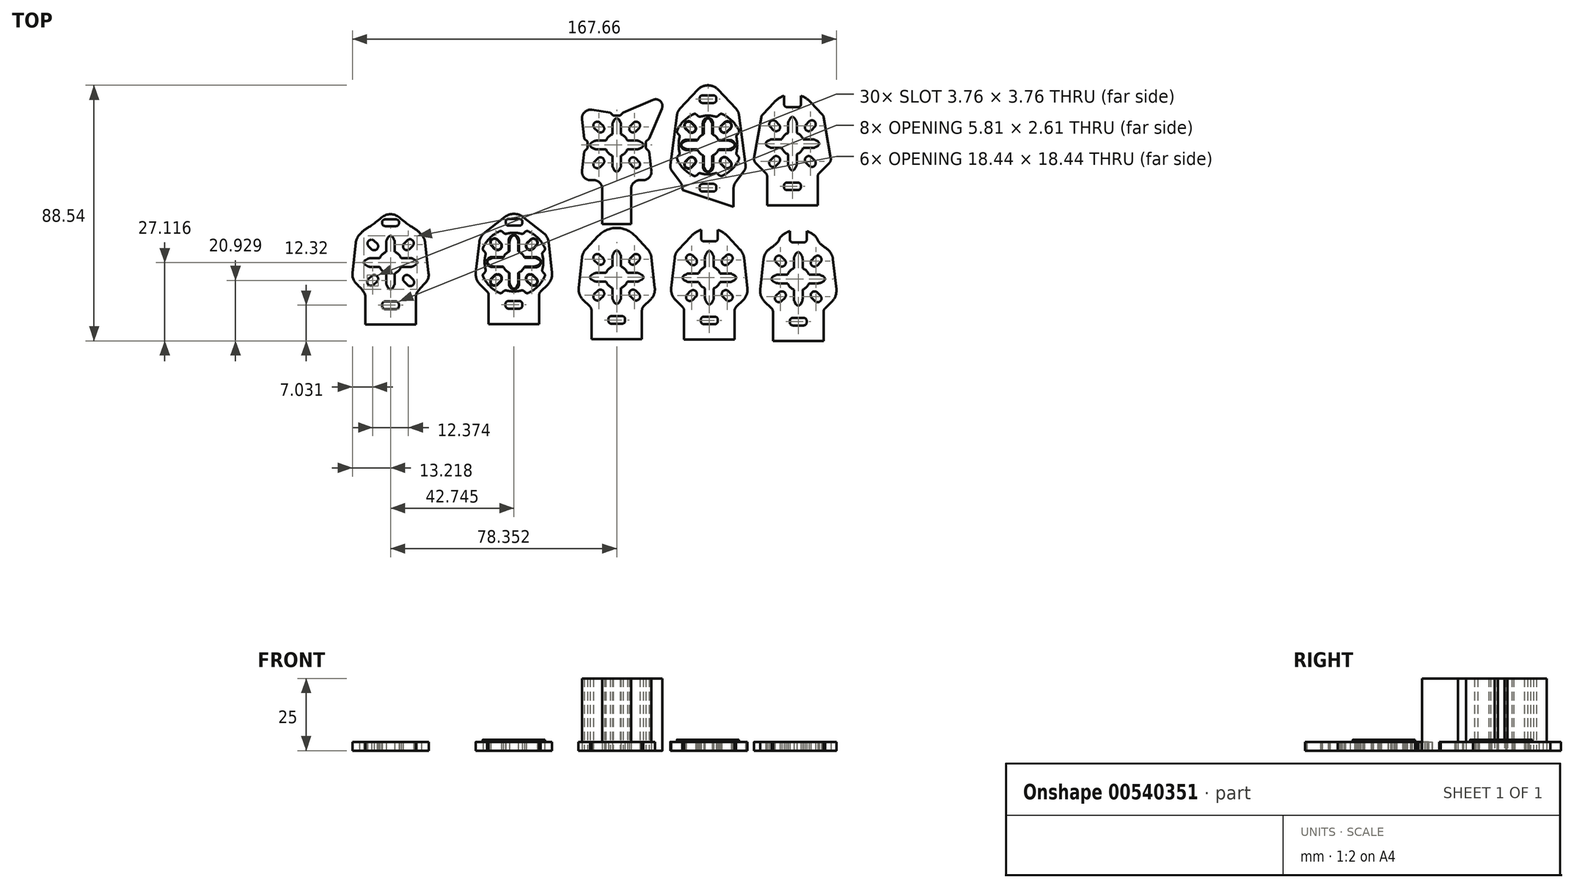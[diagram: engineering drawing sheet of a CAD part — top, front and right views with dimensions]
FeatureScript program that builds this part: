
annotation { "Feature Type Name" : "Feature", "Feature Type Description" : "" }
export const myFeature = defineFeature(function(context is Context, id is Id, definition is map)
    precondition{}
    {
        {
            var Q0;
            Q0=qCreatedBy(makeId("Top.planeOp"),FACE);
            var sketch = newSketch(context, id + "F0", { "sketchPlane" : qUnion([Q0])});
            skArc(sketch, "E0", {"start": v(6.61, -4.7) * mm, "mid": v(4.7, -4.7) * mm, "end": v(4.7, -6.61) * mm});
            skArc(sketch, "E1", {"start": v(5.76, -7.67) * mm, "mid": v(7.67, -7.67) * mm, "end": v(7.67, -5.76) * mm});
            skLineSegment(sketch, "E2", {"start": v(0, 0) * mm, "end": v(-21.23, -21.23) * mm, "construction": true});
            skLineSegment(sketch, "E3", {"start": v(4.7, -6.61) * mm, "end": v(5.76, -7.67) * mm});
            skLineSegment(sketch, "E4.MirrorCS", {"start": v(6.61, -4.7) * mm, "end": v(7.67, -5.76) * mm});
            skLineSegment(sketch, "E5.MirrorCS", {"start": v(-6.61, -4.7) * mm, "end": v(-7.67, -5.76) * mm});
            skArc(sketch, "E6.MirrorCS", {"start": v(-5.76, -7.67) * mm, "mid": v(-7.67, -7.67) * mm, "end": v(-7.67, -5.76) * mm});
            skLineSegment(sketch, "E7.MirrorCS", {"start": v(-4.7, -6.61) * mm, "end": v(-5.76, -7.67) * mm});
            skArc(sketch, "E8.MirrorCS", {"start": v(-6.61, -4.7) * mm, "mid": v(-4.7, -4.7) * mm, "end": v(-4.7, -6.61) * mm});
            skLineSegment(sketch, "E9.MirrorCS", {"start": v(-4.7, 6.61) * mm, "end": v(-5.76, 7.67) * mm});
            skLineSegment(sketch, "E10.MirrorCS", {"start": v(-6.61, 4.7) * mm, "end": v(-7.67, 5.76) * mm});
            skArc(sketch, "E11.MirrorCS", {"start": v(-6.61, 4.7) * mm, "mid": v(-4.7, 4.7) * mm, "end": v(-4.7, 6.61) * mm});
            skArc(sketch, "E12.MirrorCS", {"start": v(-5.76, 7.67) * mm, "mid": v(-7.67, 7.67) * mm, "end": v(-7.67, 5.76) * mm});
            skLineSegment(sketch, "E13.MirrorCS", {"start": v(4.7, 6.61) * mm, "end": v(5.76, 7.67) * mm});
            skLineSegment(sketch, "E14.MirrorCS", {"start": v(6.61, 4.7) * mm, "end": v(7.67, 5.76) * mm});
            skArc(sketch, "E15.MirrorCS", {"start": v(5.76, 7.67) * mm, "mid": v(7.67, 7.67) * mm, "end": v(7.67, 5.76) * mm});
            skArc(sketch, "E16.MirrorCS", {"start": v(6.61, 4.7) * mm, "mid": v(4.7, 4.7) * mm, "end": v(4.7, 6.61) * mm});
            skArc(sketch, "E17", {"start": v(1.5, -3.7) * mm, "mid": v(2.83, -2.83) * mm, "end": v(3.7, -1.5) * mm});
            skLineSegment(sketch, "E18.bottom", {"start": v(-6.98, 1.5) * mm, "end": v(-3.7, 1.5) * mm});
            skLineSegment(sketch, "E18.top", {"start": v(-6.98, -1.5) * mm, "end": v(-3.7, -1.5) * mm});
            skLineSegment(sketch, "E19.left", {"start": v(-1.5, 6.98) * mm, "end": v(-1.5, 3.7) * mm});
            skLineSegment(sketch, "E19.right", {"start": v(1.5, 6.98) * mm, "end": v(1.5, 3.7) * mm});
            skLineSegment(sketch, "E20.trimOffspring", {"start": v(3.7, -1.5) * mm, "end": v(6.98, -1.5) * mm});
            skLineSegment(sketch, "E21.trimOffspring", {"start": v(3.7, 1.5) * mm, "end": v(6.98, 1.5) * mm});
            skLineSegment(sketch, "E22.trimOffspring", {"start": v(1.5, -3.7) * mm, "end": v(1.5, -6.98) * mm});
            skLineSegment(sketch, "E23.trimOffspring", {"start": v(-1.5, -3.7) * mm, "end": v(-1.5, -6.98) * mm});
            skArc(sketch, "E24.trimOffspring", {"start": v(3.7, 1.5) * mm, "mid": v(2.83, 2.83) * mm, "end": v(1.5, 3.7) * mm});
            skArc(sketch, "E25.trimOffspring", {"start": v(-1.5, 3.7) * mm, "mid": v(-2.83, 2.83) * mm, "end": v(-3.7, 1.5) * mm});
            skArc(sketch, "E26.trimOffspring", {"start": v(-3.7, -1.5) * mm, "mid": v(-2.83, -2.83) * mm, "end": v(-1.5, -3.7) * mm});
            skArc(sketch, "E27", {"start": v(9.28, -0.51) * mm, "mid": v(9.33, -0.48) * mm, "end": v(9.38, -0.44) * mm});
            skArc(sketch, "E28.filletArc", {"start": v(6.98, -1.5) * mm, "mid": v(7.48, -1.44) * mm, "end": v(7.95, -1.25) * mm});
            skArc(sketch, "E29.filletArc", {"start": v(7.95, 1.25) * mm, "mid": v(7.48, 1.44) * mm, "end": v(6.98, 1.5) * mm});
            skArc(sketch, "E30.MirrorCS", {"start": v(-7.95, 1.25) * mm, "mid": v(-7.48, 1.44) * mm, "end": v(-6.98, 1.5) * mm});
            skArc(sketch, "E31.MirrorCS", {"start": v(-6.98, -1.5) * mm, "mid": v(-7.48, -1.44) * mm, "end": v(-7.95, -1.25) * mm});
            skArc(sketch, "E32.MirrorCS", {"start": v(-9.28, -0.51) * mm, "mid": v(-9.33, -0.48) * mm, "end": v(-9.38, -0.44) * mm});
            skArc(sketch, "E33.MirrorCS", {"start": v(1.25, -7.95) * mm, "mid": v(1.44, -7.48) * mm, "end": v(1.5, -6.98) * mm});
            skArc(sketch, "E34.MirrorCS", {"start": v(-1.5, -6.98) * mm, "mid": v(-1.44, -7.48) * mm, "end": v(-1.25, -7.95) * mm});
            skArc(sketch, "E35.MirrorCS", {"start": v(-1.5, 6.98) * mm, "mid": v(-1.44, 7.48) * mm, "end": v(-1.25, 7.95) * mm});
            skArc(sketch, "E36.MirrorCS", {"start": v(1.25, 7.95) * mm, "mid": v(1.44, 7.48) * mm, "end": v(1.5, 6.98) * mm});
            skCircle(sketch, "E37", {"center": v(0, 0) * mm, "radius": 8 * mm, "construction": true});
            skLineSegment(sketch, "E38", {"start": v(-1.25, 7.95) * mm, "end": v(-0.81, 8.74) * mm});
            skLineSegment(sketch, "E39.MirrorCS", {"start": v(-1.25, -7.95) * mm, "end": v(-0.81, -8.74) * mm});
            skLineSegment(sketch, "E40.MirrorCS", {"start": v(1.25, 7.95) * mm, "end": v(0.81, 8.74) * mm});
            skArc(sketch, "E41", {"start": v(0.81, 8.74) * mm, "mid": v(0, 9.22) * mm, "end": v(-0.81, 8.74) * mm});
            skLineSegment(sketch, "E42.MirrorCS", {"start": v(1.25, -7.95) * mm, "end": v(0.81, -8.74) * mm});
            skArc(sketch, "E43.MirrorCS", {"start": v(0.81, -8.74) * mm, "mid": v(0, -9.22) * mm, "end": v(-0.81, -8.74) * mm});
            skLineSegment(sketch, "E44.MirrorCS", {"start": v(7.95, 1.25) * mm, "end": v(8.74, 0.81) * mm});
            skLineSegment(sketch, "E45.MirrorCS", {"start": v(7.95, -1.25) * mm, "end": v(8.74, -0.81) * mm});
            skArc(sketch, "E46.MirrorCS", {"start": v(8.74, 0.81) * mm, "mid": v(9.22, 0) * mm, "end": v(8.74, -0.81) * mm});
            skLineSegment(sketch, "E47.MirrorCS", {"start": v(-7.95, 1.25) * mm, "end": v(-8.74, 0.81) * mm});
            skLineSegment(sketch, "E48.MirrorCS", {"start": v(-7.95, -1.25) * mm, "end": v(-8.74, -0.81) * mm});
            skArc(sketch, "E49.MirrorCS", {"start": v(-8.74, 0.81) * mm, "mid": v(-9.22, 0) * mm, "end": v(-8.74, -0.81) * mm});
            skPoint(sketch, "E50.visualSharp", {"position": v(-9.2, -10.96) * mm});
            skLineSegment(sketch, "E51.top", {"start": v(-5, -27.37) * mm, "end": v(5, -27.37) * mm});
            skLineSegment(sketch, "E51.left", {"start": v(-5, -14.93) * mm, "end": v(-5, -27.37) * mm});
            skLineSegment(sketch, "E51.right", {"start": v(5, -14.93) * mm, "end": v(5, -27.37) * mm});
            skPoint(sketch, "E51.middle", {"position": v(0, -19.87) * mm});
            skLineSegment(sketch, "E52.0", {"start": v(10.15, 1.17) * mm, "end": v(11.2, 2.23) * mm});
            skLineSegment(sketch, "E53.0", {"start": v(1.17, 10.15) * mm, "end": v(2.23, 11.2) * mm});
            skPoint(sketch, "E54.visualSharp", {"position": v(12.52, 12.8) * mm});
            skLineSegment(sketch, "E55.MirrorCS", {"start": v(10.15, -1.17) * mm, "end": v(11.2, -2.23) * mm});
            skLineSegment(sketch, "E56.MirrorCS", {"start": v(12.03, -8.86) * mm, "end": v(11.2, -2.23) * mm});
            skArc(sketch, "E57.MirrorCS", {"start": v(12.03, -8.86) * mm, "mid": v(11.14, -11.38) * mm, "end": v(8.6, -12.2) * mm});
            skLineSegment(sketch, "E58", {"start": v(10.15, 1.17) * mm, "end": v(10.15, -1.17) * mm});
            skArc(sketch, "E59.MirrorCS", {"start": v(-12.03, 8.86) * mm, "mid": v(-11.14, 11.38) * mm, "end": v(-8.6, 12.2) * mm});
            skLineSegment(sketch, "E60.MirrorCS", {"start": v(-2.23, 11.2) * mm, "end": v(-8.6, 12.2) * mm});
            skLineSegment(sketch, "E61.MirrorCS", {"start": v(-12.03, 8.86) * mm, "end": v(-11.2, 2.23) * mm});
            skLineSegment(sketch, "E62.MirrorCS", {"start": v(-1.17, 10.15) * mm, "end": v(-2.23, 11.2) * mm});
            skLineSegment(sketch, "E63.MirrorCS", {"start": v(-10.15, 1.17) * mm, "end": v(-11.2, 2.23) * mm});
            skLineSegment(sketch, "E64.MirrorCS", {"start": v(-10.15, 1.17) * mm, "end": v(-10.15, -1.17) * mm});
            skLineSegment(sketch, "E65.MirrorCS", {"start": v(-10.15, -1.17) * mm, "end": v(-11.2, -2.23) * mm});
            skLineSegment(sketch, "E66.MirrorCS", {"start": v(-12.03, -8.86) * mm, "end": v(-11.2, -2.23) * mm});
            skArc(sketch, "E67.MirrorCS", {"start": v(-12.03, -8.86) * mm, "mid": v(-11.14, -11.38) * mm, "end": v(-8.6, -12.2) * mm});
            skLineSegment(sketch, "E68", {"start": v(2.23, 11.2) * mm, "end": v(12.62, 15.65) * mm});
            skLineSegment(sketch, "E69.MirrorCS", {"start": v(11.2, 2.23) * mm, "end": v(15.65, 12.62) * mm});
            skArc(sketch, "E70", {"start": v(15.65, 12.62) * mm, "mid": v(15.16, 15.16) * mm, "end": v(12.62, 15.65) * mm});
            skPoint(sketch, "E54.filletArc.end.orphan", {"position": v(8.6, 12.2) * mm});
            skPoint(sketch, "E71.start.orphan", {"position": v(12.03, 8.86) * mm});
            skArc(sketch, "E72", {"start": v(8.6, -12.2) * mm, "mid": v(5.94, -13.04) * mm, "end": v(5, -15.66) * mm});
            skArc(sketch, "E73.MirrorCS", {"start": v(-8.6, -12.2) * mm, "mid": v(-5.94, -13.04) * mm, "end": v(-5, -15.66) * mm});
            skPoint(sketch, "E74.MirrorCS.end.orphan", {"position": v(-8.6, -12.2) * mm});
            skPoint(sketch, "E74.MirrorCS.start.orphan", {"position": v(-2.23, -11.2) * mm});
            skPoint(sketch, "E75.MirrorCS.start.orphan", {"position": v(-1.17, -10.15) * mm});
            skPoint(sketch, "E76.MirrorCS.end.orphan", {"position": v(2.23, -11.2) * mm});
            skPoint(sketch, "E76.MirrorCS.start.orphan", {"position": v(1.17, -10.15) * mm});
            skPoint(sketch, "E77.MirrorCS.end.orphan", {"position": v(8.6, -12.2) * mm});
            skPoint(sketch, "E78.orphan", {"position": v(5, -12.37) * mm});
            skPoint(sketch, "E79.orphan", {"position": v(-5, -12.37) * mm});
            skLineSegment(sketch, "E80", {"start": v(1.17, 10.15) * mm, "end": v(-1.17, 10.15) * mm});
            skLineSegment(sketch, "E81", {"start": v(-1.17, 10.15) * mm, "end": v(-7.48, 13.67) * mm});
            skLineSegment(sketch, "E82.MirrorCS", {"start": v(10.15, -1.17) * mm, "end": v(13.67, -7.48) * mm});
            skLineSegment(sketch, "E83.MirrorCS", {"start": v(1.17, 10.15) * mm, "end": v(7.48, 13.67) * mm});
            skSolve(sketch);
        }
        {
            var Q0;
            Q0=qCreatedBy(makeId("Top.planeOp"),FACE);
            var sketch = newSketch(context, id + "F1", { "sketchPlane" : qUnion([Q0])});
            skCircle(sketch, "E84", {"center": v(31.61, 0) * mm, "radius": 13.85 * mm, "construction": true});
            skLineSegment(sketch, "E85", {"start": v(31.61, 0) * mm, "end": v(42.92, -11.31) * mm, "construction": true});
            skArc(sketch, "E86", {"start": v(38.22, -4.7) * mm, "mid": v(36.31, -4.7) * mm, "end": v(36.31, -6.61) * mm});
            skArc(sketch, "E87", {"start": v(37.37, -7.67) * mm, "mid": v(39.28, -7.67) * mm, "end": v(39.28, -5.76) * mm});
            skLineSegment(sketch, "E88", {"start": v(-0.04, 0.14) * mm, "end": v(-0.04, -29.88) * mm, "construction": true});
            skLineSegment(sketch, "E89", {"start": v(36.31, -6.61) * mm, "end": v(37.37, -7.67) * mm});
            skLineSegment(sketch, "E90.MirrorCS", {"start": v(38.22, -4.7) * mm, "end": v(39.28, -5.76) * mm});
            skLineSegment(sketch, "E91.MirrorCS", {"start": v(25, -4.7) * mm, "end": v(23.94, -5.76) * mm});
            skArc(sketch, "E92.MirrorCS", {"start": v(25.85, -7.67) * mm, "mid": v(23.94, -7.67) * mm, "end": v(23.94, -5.76) * mm});
            skLineSegment(sketch, "E93.MirrorCS", {"start": v(26.9, -6.61) * mm, "end": v(25.85, -7.67) * mm});
            skArc(sketch, "E94.MirrorCS", {"start": v(25, -4.7) * mm, "mid": v(26.9, -4.7) * mm, "end": v(26.9, -6.61) * mm});
            skLineSegment(sketch, "E95.MirrorCS", {"start": v(26.9, 6.61) * mm, "end": v(25.85, 7.67) * mm});
            skLineSegment(sketch, "E96.MirrorCS", {"start": v(25, 4.7) * mm, "end": v(23.94, 5.76) * mm});
            skArc(sketch, "E97.MirrorCS", {"start": v(25, 4.7) * mm, "mid": v(26.9, 4.7) * mm, "end": v(26.9, 6.61) * mm});
            skArc(sketch, "E98.MirrorCS", {"start": v(25.85, 7.67) * mm, "mid": v(23.94, 7.67) * mm, "end": v(23.94, 5.76) * mm});
            skLineSegment(sketch, "E99.MirrorCS", {"start": v(36.31, 6.61) * mm, "end": v(37.37, 7.67) * mm});
            skLineSegment(sketch, "E100.MirrorCS", {"start": v(38.22, 4.7) * mm, "end": v(39.28, 5.76) * mm});
            skArc(sketch, "E101.MirrorCS", {"start": v(37.37, 7.67) * mm, "mid": v(39.28, 7.67) * mm, "end": v(39.28, 5.76) * mm});
            skArc(sketch, "E102.MirrorCS", {"start": v(38.22, 4.7) * mm, "mid": v(36.31, 4.7) * mm, "end": v(36.31, 6.61) * mm});
            skLineSegment(sketch, "E103", {"start": v(42.35, 10.4) * mm, "end": v(44.62, -6.92) * mm});
            skLineSegment(sketch, "E104", {"start": v(34.52, 16.16) * mm, "end": v(34.52, 15.55) * mm});
            skLineSegment(sketch, "E105", {"start": v(28.7, 16.16) * mm, "end": v(28.7, 15.55) * mm});
            skArc(sketch, "E106", {"start": v(33.11, -3.7) * mm, "mid": v(34.44, -2.83) * mm, "end": v(35.32, -1.5) * mm});
            skLineSegment(sketch, "E107.bottom", {"start": v(24.63, 1.5) * mm, "end": v(27.9, 1.5) * mm});
            skLineSegment(sketch, "E107.top", {"start": v(24.63, -1.5) * mm, "end": v(27.9, -1.5) * mm});
            skLineSegment(sketch, "E108.left", {"start": v(30.11, 6.98) * mm, "end": v(30.11, 3.7) * mm});
            skLineSegment(sketch, "E108.right", {"start": v(33.11, 6.98) * mm, "end": v(33.11, 3.7) * mm});
            skLineSegment(sketch, "E109.trimOffspring", {"start": v(35.32, -1.5) * mm, "end": v(38.6, -1.5) * mm});
            skLineSegment(sketch, "E110.trimOffspring", {"start": v(35.32, 1.5) * mm, "end": v(38.6, 1.5) * mm});
            skLineSegment(sketch, "E111.trimOffspring", {"start": v(33.11, -3.7) * mm, "end": v(33.11, -6.98) * mm});
            skLineSegment(sketch, "E112.trimOffspring", {"start": v(30.11, -3.7) * mm, "end": v(30.11, -6.98) * mm});
            skArc(sketch, "E113.trimOffspring", {"start": v(35.32, 1.5) * mm, "mid": v(34.44, 2.83) * mm, "end": v(33.11, 3.7) * mm});
            skArc(sketch, "E114.trimOffspring", {"start": v(30.11, 3.7) * mm, "mid": v(28.78, 2.83) * mm, "end": v(27.9, 1.5) * mm});
            skArc(sketch, "E115.trimOffspring", {"start": v(27.9, -1.5) * mm, "mid": v(28.78, -2.83) * mm, "end": v(30.11, -3.7) * mm});
            skArc(sketch, "E116", {"start": v(40.89, -0.51) * mm, "mid": v(40.94, -0.48) * mm, "end": v(41, -0.44) * mm});
            skArc(sketch, "E117.filletArc", {"start": v(38.6, -1.5) * mm, "mid": v(39.1, -1.44) * mm, "end": v(39.56, -1.25) * mm});
            skArc(sketch, "E118.filletArc", {"start": v(39.56, 1.25) * mm, "mid": v(39.1, 1.44) * mm, "end": v(38.6, 1.5) * mm});
            skArc(sketch, "E119.MirrorCS", {"start": v(23.66, 1.25) * mm, "mid": v(24.13, 1.44) * mm, "end": v(24.63, 1.5) * mm});
            skArc(sketch, "E120.MirrorCS", {"start": v(24.63, -1.5) * mm, "mid": v(24.13, -1.44) * mm, "end": v(23.66, -1.25) * mm});
            skArc(sketch, "E121.MirrorCS", {"start": v(22.33, -0.51) * mm, "mid": v(22.28, -0.48) * mm, "end": v(22.23, -0.44) * mm});
            skArc(sketch, "E122.MirrorCS", {"start": v(32.86, -7.95) * mm, "mid": v(33.05, -7.48) * mm, "end": v(33.11, -6.98) * mm});
            skArc(sketch, "E123.MirrorCS", {"start": v(30.11, -6.98) * mm, "mid": v(30.17, -7.48) * mm, "end": v(30.36, -7.95) * mm});
            skArc(sketch, "E124.MirrorCS", {"start": v(30.11, 6.98) * mm, "mid": v(30.17, 7.48) * mm, "end": v(30.36, 7.95) * mm});
            skArc(sketch, "E125.MirrorCS", {"start": v(32.86, 7.95) * mm, "mid": v(33.05, 7.48) * mm, "end": v(33.11, 6.98) * mm});
            skArc(sketch, "E126.filletArc", {"start": v(33.52, 14.55) * mm, "mid": v(34.22, 14.84) * mm, "end": v(34.52, 15.55) * mm});
            skArc(sketch, "E127.filletArc", {"start": v(28.7, 15.55) * mm, "mid": v(29, 14.84) * mm, "end": v(29.7, 14.55) * mm});
            skCircle(sketch, "E128", {"center": v(31.61, 0) * mm, "radius": 8 * mm, "construction": true});
            skLineSegment(sketch, "E129", {"start": v(41.3, 12.62) * mm, "end": v(35.12, 19.16) * mm});
            skArc(sketch, "E130.filletArc", {"start": v(42.35, 10.4) * mm, "mid": v(42, 11.59) * mm, "end": v(41.3, 12.62) * mm});
            skLineSegment(sketch, "E131.MirrorCS", {"start": v(21.93, 12.62) * mm, "end": v(28.1, 19.16) * mm});
            skLineSegment(sketch, "E132", {"start": v(44.04, -9.12) * mm, "end": v(41.43, -12.56) * mm});
            skArc(sketch, "E133.filletArc", {"start": v(44.04, -9.12) * mm, "mid": v(44.55, -8.08) * mm, "end": v(44.62, -6.92) * mm});
            skArc(sketch, "E134", {"start": v(35.12, 19.16) * mm, "mid": v(31.61, 20.68) * mm, "end": v(28.1, 19.16) * mm});
            skLineSegment(sketch, "E135", {"start": v(40.41, -15.58) * mm, "end": v(40.41, -21.43) * mm});
            skArc(sketch, "E136.filletArc", {"start": v(41.43, -12.56) * mm, "mid": v(40.67, -14) * mm, "end": v(40.41, -15.58) * mm});
            skLineSegment(sketch, "E137.MirrorCS", {"start": v(20.87, 10.4) * mm, "end": v(18.6, -6.92) * mm});
            skArc(sketch, "E138.MirrorCS", {"start": v(20.87, 10.4) * mm, "mid": v(21.23, 11.59) * mm, "end": v(21.93, 12.62) * mm});
            skArc(sketch, "E139.MirrorCS", {"start": v(19.18, -9.12) * mm, "mid": v(18.67, -8.08) * mm, "end": v(18.6, -6.92) * mm});
            skLineSegment(sketch, "E140.MirrorCS", {"start": v(19.18, -9.12) * mm, "end": v(21.8, -12.56) * mm});
            skArc(sketch, "E141.MirrorCS", {"start": v(21.8, -12.56) * mm, "mid": v(22.55, -14) * mm, "end": v(22.8, -15.58) * mm});
            skLineSegment(sketch, "E142.MirrorCS", {"start": v(4.75, -17.1) * mm, "end": v(8.9, -21.24) * mm});
            skLineSegment(sketch, "E143", {"start": v(29.7, 14.55) * mm, "end": v(33.52, 14.55) * mm});
            skLineSegment(sketch, "E144", {"start": v(31.61, 15.86) * mm, "end": v(29.02, 15.86) * mm, "construction": true});
            skArc(sketch, "E145.MirrorCS", {"start": v(33.52, 17.16) * mm, "mid": v(34.22, 16.87) * mm, "end": v(34.52, 16.16) * mm});
            skArc(sketch, "E146.MirrorCS", {"start": v(28.7, 16.16) * mm, "mid": v(29, 16.87) * mm, "end": v(29.7, 17.16) * mm});
            skLineSegment(sketch, "E147.MirrorCS", {"start": v(29.7, 17.16) * mm, "end": v(33.52, 17.16) * mm});
            skLineSegment(sketch, "E148.MirrorCS", {"start": v(29.7, -13.5) * mm, "end": v(33.52, -13.5) * mm});
            skArc(sketch, "E149.MirrorCS", {"start": v(28.7, -14.5) * mm, "mid": v(29, -13.78) * mm, "end": v(29.7, -13.5) * mm});
            skArc(sketch, "E150.MirrorCS", {"start": v(33.52, -13.5) * mm, "mid": v(34.22, -13.78) * mm, "end": v(34.52, -14.5) * mm});
            skLineSegment(sketch, "E151.MirrorCS", {"start": v(29.7, -16.1) * mm, "end": v(33.52, -16.1) * mm});
            skArc(sketch, "E152.MirrorCS", {"start": v(28.7, -15.1) * mm, "mid": v(29, -15.8) * mm, "end": v(29.7, -16.1) * mm});
            skArc(sketch, "E153.MirrorCS", {"start": v(33.52, -16.1) * mm, "mid": v(34.22, -15.8) * mm, "end": v(34.52, -15.1) * mm});
            skLineSegment(sketch, "E154.MirrorCS", {"start": v(34.52, -15.1) * mm, "end": v(34.52, -14.5) * mm});
            skLineSegment(sketch, "E155.MirrorCS", {"start": v(28.7, -15.1) * mm, "end": v(28.7, -14.5) * mm});
            skLineSegment(sketch, "E156", {"start": v(30.36, 7.95) * mm, "end": v(30.8, 8.74) * mm});
            skLineSegment(sketch, "E157.trimOffspring", {"start": v(31.61, -9) * mm, "end": v(31.61, 20.87) * mm, "construction": true});
            skLineSegment(sketch, "E158.MirrorCS", {"start": v(30.36, -7.95) * mm, "end": v(30.8, -8.74) * mm});
            skLineSegment(sketch, "E159.MirrorCS", {"start": v(32.86, 7.95) * mm, "end": v(32.42, 8.74) * mm});
            skArc(sketch, "E160", {"start": v(32.42, 8.74) * mm, "mid": v(31.61, 9.22) * mm, "end": v(30.8, 8.74) * mm});
            skLineSegment(sketch, "E161.MirrorCS", {"start": v(32.86, -7.95) * mm, "end": v(32.42, -8.74) * mm});
            skArc(sketch, "E162.MirrorCS", {"start": v(32.42, -8.74) * mm, "mid": v(31.61, -9.22) * mm, "end": v(30.8, -8.74) * mm});
            skLineSegment(sketch, "E163.MirrorCS", {"start": v(39.56, 1.25) * mm, "end": v(40.35, 0.81) * mm});
            skLineSegment(sketch, "E164.MirrorCS", {"start": v(39.56, -1.25) * mm, "end": v(40.35, -0.81) * mm});
            skArc(sketch, "E165.MirrorCS", {"start": v(40.35, 0.81) * mm, "mid": v(40.83, 0) * mm, "end": v(40.35, -0.81) * mm});
            skLineSegment(sketch, "E166.MirrorCS", {"start": v(23.66, 1.25) * mm, "end": v(22.87, 0.81) * mm});
            skLineSegment(sketch, "E167.MirrorCS", {"start": v(23.66, -1.25) * mm, "end": v(22.87, -0.81) * mm});
            skArc(sketch, "E168.MirrorCS", {"start": v(22.87, 0.81) * mm, "mid": v(22.4, 0) * mm, "end": v(22.87, -0.81) * mm});
            skLineSegment(sketch, "E169", {"start": v(22.8, -15.58) * mm, "end": v(40.41, -21.43) * mm});
            skSolve(sketch);
        }
        {
            var Q0;
            Q0=qCreatedBy(makeId("Top.planeOp"),FACE);
            var sketch = newSketch(context, id + "F2", { "sketchPlane" : qUnion([Q0])});
            skLineSegment(sketch, "E170", {"start": v(60.87, 0.46) * mm, "end": v(72.19, -10.86) * mm, "construction": true});
            skArc(sketch, "E171", {"start": v(67.48, -4.24) * mm, "mid": v(65.58, -4.24) * mm, "end": v(65.58, -6.15) * mm});
            skArc(sketch, "E172", {"start": v(66.64, -7.21) * mm, "mid": v(68.54, -7.21) * mm, "end": v(68.54, -5.3) * mm});
            skLineSegment(sketch, "E173", {"start": v(65.58, -6.15) * mm, "end": v(66.64, -7.21) * mm});
            skLineSegment(sketch, "E174.MirrorCS", {"start": v(67.48, -4.24) * mm, "end": v(68.54, -5.3) * mm});
            skLineSegment(sketch, "E175.MirrorCS", {"start": v(54.26, -4.24) * mm, "end": v(53.2, -5.3) * mm});
            skArc(sketch, "E176.MirrorCS", {"start": v(55.1, -7.21) * mm, "mid": v(53.2, -7.21) * mm, "end": v(53.2, -5.3) * mm});
            skLineSegment(sketch, "E177.MirrorCS", {"start": v(56.17, -6.15) * mm, "end": v(55.1, -7.21) * mm});
            skArc(sketch, "E178.MirrorCS", {"start": v(54.26, -4.24) * mm, "mid": v(56.17, -4.24) * mm, "end": v(56.17, -6.15) * mm});
            skLineSegment(sketch, "E179.MirrorCS", {"start": v(56.17, 7.07) * mm, "end": v(55.1, 8.13) * mm});
            skLineSegment(sketch, "E180.MirrorCS", {"start": v(54.26, 5.16) * mm, "end": v(53.2, 6.22) * mm});
            skArc(sketch, "E181.MirrorCS", {"start": v(54.26, 5.16) * mm, "mid": v(56.17, 5.16) * mm, "end": v(56.17, 7.07) * mm});
            skArc(sketch, "E182.MirrorCS", {"start": v(55.1, 8.13) * mm, "mid": v(53.2, 8.13) * mm, "end": v(53.2, 6.22) * mm});
            skLineSegment(sketch, "E183.MirrorCS", {"start": v(65.58, 7.07) * mm, "end": v(66.64, 8.13) * mm});
            skLineSegment(sketch, "E184.MirrorCS", {"start": v(67.48, 5.16) * mm, "end": v(68.54, 6.22) * mm});
            skArc(sketch, "E185.MirrorCS", {"start": v(66.64, 8.13) * mm, "mid": v(68.54, 8.13) * mm, "end": v(68.54, 6.22) * mm});
            skArc(sketch, "E186.MirrorCS", {"start": v(67.48, 5.16) * mm, "mid": v(65.58, 5.16) * mm, "end": v(65.58, 7.07) * mm});
            skLineSegment(sketch, "E187", {"start": v(63.8, 14.7) * mm, "end": v(63.8, 14.09) * mm});
            skLineSegment(sketch, "E188", {"start": v(58, 14.7) * mm, "end": v(58, 14.09) * mm});
            skArc(sketch, "E189", {"start": v(62.37, -3.25) * mm, "mid": v(63.7, -2.37) * mm, "end": v(64.58, -1.04) * mm});
            skLineSegment(sketch, "E190.bottom", {"start": v(53.9, 1.96) * mm, "end": v(57.16, 1.96) * mm});
            skLineSegment(sketch, "E190.top", {"start": v(53.9, -1.04) * mm, "end": v(57.16, -1.04) * mm});
            skLineSegment(sketch, "E191.left", {"start": v(59.37, 7.44) * mm, "end": v(59.37, 4.17) * mm});
            skLineSegment(sketch, "E191.right", {"start": v(62.37, 7.44) * mm, "end": v(62.37, 4.17) * mm});
            skLineSegment(sketch, "E192.trimOffspring", {"start": v(64.58, -1.04) * mm, "end": v(67.86, -1.04) * mm});
            skLineSegment(sketch, "E193.trimOffspring", {"start": v(64.58, 1.96) * mm, "end": v(67.86, 1.96) * mm});
            skLineSegment(sketch, "E194.trimOffspring", {"start": v(62.37, -3.25) * mm, "end": v(62.37, -6.52) * mm});
            skLineSegment(sketch, "E195.trimOffspring", {"start": v(59.37, -3.25) * mm, "end": v(59.37, -6.52) * mm});
            skArc(sketch, "E196.trimOffspring", {"start": v(64.58, 1.96) * mm, "mid": v(63.7, 3.29) * mm, "end": v(62.37, 4.17) * mm});
            skArc(sketch, "E197.trimOffspring", {"start": v(59.37, 4.17) * mm, "mid": v(58.04, 3.29) * mm, "end": v(57.16, 1.96) * mm});
            skArc(sketch, "E198.trimOffspring", {"start": v(57.16, -1.04) * mm, "mid": v(58.04, -2.37) * mm, "end": v(59.37, -3.25) * mm});
            skArc(sketch, "E199", {"start": v(70.15, -0.06) * mm, "mid": v(70.2, -0.02) * mm, "end": v(70.25, 0.02) * mm});
            skArc(sketch, "E200.filletArc", {"start": v(67.86, -1.04) * mm, "mid": v(68.36, -0.98) * mm, "end": v(68.83, -0.8) * mm});
            skArc(sketch, "E201.filletArc", {"start": v(68.83, 1.7) * mm, "mid": v(68.36, 1.9) * mm, "end": v(67.86, 1.96) * mm});
            skArc(sketch, "E202.MirrorCS", {"start": v(52.92, 1.7) * mm, "mid": v(53.39, 1.9) * mm, "end": v(53.9, 1.96) * mm});
            skArc(sketch, "E203.MirrorCS", {"start": v(53.9, -1.04) * mm, "mid": v(53.39, -0.98) * mm, "end": v(52.92, -0.8) * mm});
            skArc(sketch, "E204.MirrorCS", {"start": v(51.6, -0.06) * mm, "mid": v(51.54, -0.02) * mm, "end": v(51.5, 0.02) * mm});
            skArc(sketch, "E205.MirrorCS", {"start": v(62.12, -7.5) * mm, "mid": v(62.3, -7.03) * mm, "end": v(62.37, -6.52) * mm});
            skArc(sketch, "E206.MirrorCS", {"start": v(59.37, -6.52) * mm, "mid": v(59.44, -7.03) * mm, "end": v(59.62, -7.5) * mm});
            skArc(sketch, "E207.MirrorCS", {"start": v(59.37, 7.44) * mm, "mid": v(59.44, 7.94) * mm, "end": v(59.62, 8.41) * mm});
            skArc(sketch, "E208.MirrorCS", {"start": v(62.12, 8.41) * mm, "mid": v(62.3, 7.94) * mm, "end": v(62.37, 7.44) * mm});
            skArc(sketch, "E209.filletArc", {"start": v(62.8, 13.09) * mm, "mid": v(63.52, 13.38) * mm, "end": v(63.8, 14.09) * mm});
            skArc(sketch, "E210.filletArc", {"start": v(58, 14.09) * mm, "mid": v(58.3, 13.38) * mm, "end": v(59, 13.09) * mm});
            skCircle(sketch, "E211", {"center": v(60.87, 0.46) * mm, "radius": 8 * mm, "construction": true});
            skLineSegment(sketch, "E212.MirrorCS", {"start": v(52.13, -11.05) * mm, "end": v(52.13, -20.98) * mm});
            skLineSegment(sketch, "E213", {"start": v(59, 13.09) * mm, "end": v(62.8, 13.09) * mm});
            skLineSegment(sketch, "E214.MirrorCS", {"start": v(58.97, -13.03) * mm, "end": v(62.78, -13.03) * mm});
            skArc(sketch, "E215.MirrorCS", {"start": v(57.97, -14.03) * mm, "mid": v(58.26, -13.33) * mm, "end": v(58.97, -13.03) * mm});
            skArc(sketch, "E216.MirrorCS", {"start": v(62.78, -13.03) * mm, "mid": v(63.48, -13.33) * mm, "end": v(63.78, -14.03) * mm});
            skLineSegment(sketch, "E217.MirrorCS", {"start": v(58.97, -15.64) * mm, "end": v(62.78, -15.64) * mm});
            skArc(sketch, "E218.MirrorCS", {"start": v(57.97, -14.64) * mm, "mid": v(58.26, -15.35) * mm, "end": v(58.97, -15.64) * mm});
            skArc(sketch, "E219.MirrorCS", {"start": v(62.78, -15.64) * mm, "mid": v(63.48, -15.35) * mm, "end": v(63.78, -14.64) * mm});
            skLineSegment(sketch, "E220.MirrorCS", {"start": v(63.78, -14.64) * mm, "end": v(63.78, -14.03) * mm});
            skLineSegment(sketch, "E221.MirrorCS", {"start": v(57.97, -14.64) * mm, "end": v(57.97, -14.03) * mm});
            skLineSegment(sketch, "E222", {"start": v(59.62, 8.41) * mm, "end": v(60.06, 9.2) * mm});
            skLineSegment(sketch, "E223.trimOffspring", {"start": v(60.87, -8.53) * mm, "end": v(60.87, 21.33) * mm, "construction": true});
            skLineSegment(sketch, "E224.MirrorCS", {"start": v(59.62, -7.5) * mm, "end": v(60.06, -8.28) * mm});
            skLineSegment(sketch, "E225.MirrorCS", {"start": v(62.12, 8.41) * mm, "end": v(61.68, 9.2) * mm});
            skArc(sketch, "E226", {"start": v(61.68, 9.2) * mm, "mid": v(60.87, 9.68) * mm, "end": v(60.06, 9.2) * mm});
            skLineSegment(sketch, "E227.MirrorCS", {"start": v(62.12, -7.5) * mm, "end": v(61.68, -8.28) * mm});
            skArc(sketch, "E228.MirrorCS", {"start": v(61.68, -8.28) * mm, "mid": v(60.87, -8.76) * mm, "end": v(60.06, -8.28) * mm});
            skLineSegment(sketch, "E229.MirrorCS", {"start": v(68.83, 1.7) * mm, "end": v(69.61, 1.27) * mm});
            skLineSegment(sketch, "E230.MirrorCS", {"start": v(68.83, -0.8) * mm, "end": v(69.61, -0.35) * mm});
            skArc(sketch, "E231.MirrorCS", {"start": v(69.61, 1.27) * mm, "mid": v(70.1, 0.46) * mm, "end": v(69.61, -0.35) * mm});
            skLineSegment(sketch, "E232.MirrorCS", {"start": v(52.92, 1.7) * mm, "end": v(52.13, 1.27) * mm});
            skLineSegment(sketch, "E233.MirrorCS", {"start": v(52.92, -0.8) * mm, "end": v(52.13, -0.35) * mm});
            skArc(sketch, "E234.MirrorCS", {"start": v(52.13, 1.27) * mm, "mid": v(51.65, 0.46) * mm, "end": v(52.13, -0.35) * mm});
            skPoint(sketch, "E235.visualSharp", {"position": v(49.04, 8.46) * mm});
            skPoint(sketch, "E236.endSnap0", {"position": v(56.17, -4.24) * mm});
            skPoint(sketch, "E237.visualSharp", {"position": v(52.13, -10.28) * mm});
            skArc(sketch, "E237.filletArc", {"start": v(52.13, -11.05) * mm, "mid": v(52, -10.33) * mm, "end": v(51.62, -9.71) * mm});
            skArc(sketch, "E238.MirrorCS", {"start": v(69.62, -11.05) * mm, "mid": v(69.75, -10.33) * mm, "end": v(70.13, -9.71) * mm});
            skLineSegment(sketch, "E239.MirrorCS", {"start": v(69.62, -11.05) * mm, "end": v(69.62, -20.98) * mm});
            skLineSegment(sketch, "E240", {"start": v(52.13, -20.98) * mm, "end": v(69.62, -20.98) * mm});
            skPoint(sketch, "E241.visualSharp", {"position": v(55.95, 13.96) * mm});
            skPoint(sketch, "E242.visualSharp", {"position": v(57.8, 17.35) * mm});
            skLineSegment(sketch, "E243", {"start": v(54.48, 14.76) * mm, "end": v(50.58, 10.6) * mm});
            skPoint(sketch, "E244.visualSharp", {"position": v(47.42, -5.57) * mm});
            skPoint(sketch, "E245.visualSharp", {"position": v(49.04, 8.96) * mm});
            skArc(sketch, "E245.filletArc", {"start": v(48.86, 7.35) * mm, "mid": v(48.86, 7.33) * mm, "end": v(48.85, 7.3) * mm});
            skLineSegment(sketch, "E246.MirrorCS", {"start": v(70.13, -9.71) * mm, "end": v(70.59, -9.26) * mm});
            skPoint(sketch, "E247.visualSharp", {"position": v(64.07, 17.1) * mm});
            skArc(sketch, "E248", {"start": v(54.48, 14.76) * mm, "mid": v(56.1, 16.12) * mm, "end": v(58, 17.05) * mm});
            skLineSegment(sketch, "E249", {"start": v(58, 14.7) * mm, "end": v(58, 17.05) * mm});
            skLineSegment(sketch, "E250", {"start": v(63.8, 14.7) * mm, "end": v(63.8, 17.03) * mm});
            skArc(sketch, "E251.trimOffspring", {"start": v(63.8, 17.03) * mm, "mid": v(65.67, 16.1) * mm, "end": v(67.27, 14.76) * mm});
            skPoint(sketch, "E252.visualSharp", {"position": v(77.48, -5.66) * mm});
            skPoint(sketch, "E253.end.orphan", {"position": v(47.69, -3.16) * mm});
            skLineSegment(sketch, "E254", {"start": v(51.62, -9.71) * mm, "end": v(48.17, -6.3) * mm});
            skLineSegment(sketch, "E255", {"start": v(50.07, 9.58) * mm, "end": v(47.6, -4.54) * mm});
            skArc(sketch, "E256.filletArc", {"start": v(47.6, -4.54) * mm, "mid": v(47.66, -5.49) * mm, "end": v(48.17, -6.3) * mm});
            skPoint(sketch, "E257.visualSharp", {"position": v(50.17, 10.17) * mm});
            skArc(sketch, "E257.filletArc", {"start": v(50.58, 10.6) * mm, "mid": v(50.25, 10.13) * mm, "end": v(50.07, 9.58) * mm});
            skPoint(sketch, "E258.MirrorCS.end.orphan", {"position": v(71.57, 10.17) * mm});
            skPoint(sketch, "E259.MirrorCS.end.orphan", {"position": v(72.9, 7.3) * mm});
            skPoint(sketch, "E260.MirrorCS.end.orphan", {"position": v(74.06, -3.16) * mm});
            skLineSegment(sketch, "E261.MirrorCS", {"start": v(71.67, 9.58) * mm, "end": v(74.15, -4.54) * mm});
            skLineSegment(sketch, "E262.MirrorCS", {"start": v(70.13, -9.71) * mm, "end": v(73.58, -6.3) * mm});
            skArc(sketch, "E263.MirrorCS", {"start": v(74.15, -4.54) * mm, "mid": v(74.08, -5.49) * mm, "end": v(73.58, -6.3) * mm});
            skArc(sketch, "E264.MirrorCS", {"start": v(71.16, 10.6) * mm, "mid": v(71.5, 10.13) * mm, "end": v(71.67, 9.58) * mm});
            skLineSegment(sketch, "E265.MirrorCS", {"start": v(67.27, 14.76) * mm, "end": v(71.16, 10.6) * mm});
            skCircle(sketch, "E266", {"center": v(60.87, 0.46) * mm, "radius": 13.95 * mm, "construction": true});
            skSolve(sketch);
        }
        {
            var Q0;
            Q0=qCreatedBy(makeId("Top.planeOp"),FACE);
            var sketch = newSketch(context, id + "F3", { "sketchPlane" : qUnion([Q0])});
            skCircle(sketch, "E267", {"center": v(0, -45.84) * mm, "radius": 13.85 * mm, "construction": true});
            skLineSegment(sketch, "E268", {"start": v(0, -45.84) * mm, "end": v(11.31, -57.15) * mm, "construction": true});
            skArc(sketch, "E269", {"start": v(6.61, -50.54) * mm, "mid": v(4.7, -50.54) * mm, "end": v(4.7, -52.45) * mm});
            skArc(sketch, "E270", {"start": v(5.76, -53.5) * mm, "mid": v(7.67, -53.5) * mm, "end": v(7.67, -51.6) * mm});
            skLineSegment(sketch, "E271", {"start": v(4.7, -52.45) * mm, "end": v(5.76, -53.5) * mm});
            skLineSegment(sketch, "E272.MirrorCS", {"start": v(6.61, -50.54) * mm, "end": v(7.67, -51.6) * mm});
            skLineSegment(sketch, "E273.MirrorCS", {"start": v(-6.61, -50.54) * mm, "end": v(-7.67, -51.6) * mm});
            skArc(sketch, "E274.MirrorCS", {"start": v(-5.76, -53.5) * mm, "mid": v(-7.67, -53.5) * mm, "end": v(-7.67, -51.6) * mm});
            skLineSegment(sketch, "E275.MirrorCS", {"start": v(-4.7, -52.45) * mm, "end": v(-5.76, -53.5) * mm});
            skArc(sketch, "E276.MirrorCS", {"start": v(-6.61, -50.54) * mm, "mid": v(-4.7, -50.54) * mm, "end": v(-4.7, -52.45) * mm});
            skLineSegment(sketch, "E277.MirrorCS", {"start": v(-4.7, -39.22) * mm, "end": v(-5.76, -38.16) * mm});
            skLineSegment(sketch, "E278.MirrorCS", {"start": v(-6.61, -41.13) * mm, "end": v(-7.67, -40.07) * mm});
            skArc(sketch, "E279.MirrorCS", {"start": v(-6.61, -41.13) * mm, "mid": v(-4.7, -41.13) * mm, "end": v(-4.7, -39.22) * mm});
            skArc(sketch, "E280.MirrorCS", {"start": v(-5.76, -38.16) * mm, "mid": v(-7.67, -38.16) * mm, "end": v(-7.67, -40.07) * mm});
            skLineSegment(sketch, "E281.MirrorCS", {"start": v(4.7, -39.22) * mm, "end": v(5.76, -38.16) * mm});
            skLineSegment(sketch, "E282.MirrorCS", {"start": v(6.61, -41.13) * mm, "end": v(7.67, -40.07) * mm});
            skArc(sketch, "E283.MirrorCS", {"start": v(5.76, -38.16) * mm, "mid": v(7.67, -38.16) * mm, "end": v(7.67, -40.07) * mm});
            skArc(sketch, "E284.MirrorCS", {"start": v(6.61, -41.13) * mm, "mid": v(4.7, -41.13) * mm, "end": v(4.7, -39.22) * mm});
            skArc(sketch, "E285", {"start": v(1.5, -49.54) * mm, "mid": v(2.83, -48.66) * mm, "end": v(3.7, -47.34) * mm});
            skLineSegment(sketch, "E286.bottom", {"start": v(-6.98, -44.34) * mm, "end": v(-3.7, -44.34) * mm});
            skLineSegment(sketch, "E286.top", {"start": v(-6.98, -47.34) * mm, "end": v(-3.7, -47.34) * mm});
            skLineSegment(sketch, "E287.left", {"start": v(-1.5, -38.85) * mm, "end": v(-1.5, -42.13) * mm});
            skLineSegment(sketch, "E287.right", {"start": v(1.5, -38.85) * mm, "end": v(1.5, -42.13) * mm});
            skLineSegment(sketch, "E288.trimOffspring", {"start": v(3.7, -47.34) * mm, "end": v(6.98, -47.34) * mm});
            skLineSegment(sketch, "E289.trimOffspring", {"start": v(3.7, -44.34) * mm, "end": v(6.98, -44.34) * mm});
            skLineSegment(sketch, "E290.trimOffspring", {"start": v(1.5, -49.54) * mm, "end": v(1.5, -52.82) * mm});
            skLineSegment(sketch, "E291.trimOffspring", {"start": v(-1.5, -49.54) * mm, "end": v(-1.5, -52.82) * mm});
            skArc(sketch, "E292.trimOffspring", {"start": v(3.7, -44.34) * mm, "mid": v(2.83, -43) * mm, "end": v(1.5, -42.13) * mm});
            skArc(sketch, "E293.trimOffspring", {"start": v(-1.5, -42.13) * mm, "mid": v(-2.83, -43) * mm, "end": v(-3.7, -44.34) * mm});
            skArc(sketch, "E294.trimOffspring", {"start": v(-3.7, -47.34) * mm, "mid": v(-2.83, -48.66) * mm, "end": v(-1.5, -49.54) * mm});
            skArc(sketch, "E295", {"start": v(9.28, -46.35) * mm, "mid": v(9.33, -46.32) * mm, "end": v(9.38, -46.28) * mm});
            skArc(sketch, "E296.filletArc", {"start": v(6.98, -47.34) * mm, "mid": v(7.48, -47.27) * mm, "end": v(7.95, -47.08) * mm});
            skArc(sketch, "E297.filletArc", {"start": v(7.95, -44.59) * mm, "mid": v(7.48, -44.4) * mm, "end": v(6.98, -44.34) * mm});
            skArc(sketch, "E298.MirrorCS", {"start": v(-7.95, -44.59) * mm, "mid": v(-7.48, -44.4) * mm, "end": v(-6.98, -44.34) * mm});
            skArc(sketch, "E299.MirrorCS", {"start": v(-6.98, -47.34) * mm, "mid": v(-7.48, -47.27) * mm, "end": v(-7.95, -47.08) * mm});
            skArc(sketch, "E300.MirrorCS", {"start": v(-9.28, -46.35) * mm, "mid": v(-9.33, -46.32) * mm, "end": v(-9.38, -46.28) * mm});
            skArc(sketch, "E301.MirrorCS", {"start": v(1.25, -53.79) * mm, "mid": v(1.44, -53.32) * mm, "end": v(1.5, -52.82) * mm});
            skArc(sketch, "E302.MirrorCS", {"start": v(-1.5, -52.82) * mm, "mid": v(-1.44, -53.32) * mm, "end": v(-1.25, -53.79) * mm});
            skArc(sketch, "E303.MirrorCS", {"start": v(-1.5, -38.85) * mm, "mid": v(-1.44, -38.35) * mm, "end": v(-1.25, -37.88) * mm});
            skArc(sketch, "E304.MirrorCS", {"start": v(1.25, -37.88) * mm, "mid": v(1.44, -38.35) * mm, "end": v(1.5, -38.85) * mm});
            skArc(sketch, "E305.filletArc", {"start": v(2.93, -32.3) * mm, "mid": v(2.94, -32.25) * mm, "end": v(2.94, -32.2) * mm});
            skArc(sketch, "E306.filletArc", {"start": v(-2.87, -32.2) * mm, "mid": v(-2.87, -32.25) * mm, "end": v(-2.87, -32.29) * mm});
            skCircle(sketch, "E307", {"center": v(0, -45.84) * mm, "radius": 8 * mm, "construction": true});
            skLineSegment(sketch, "E308.MirrorCS", {"start": v(-8.74, -57.34) * mm, "end": v(-8.74, -67.27) * mm});
            skLineSegment(sketch, "E309.MirrorCS", {"start": v(-1.9, -59.33) * mm, "end": v(1.9, -59.33) * mm});
            skArc(sketch, "E310.MirrorCS", {"start": v(-2.9, -60.33) * mm, "mid": v(-2.61, -59.62) * mm, "end": v(-1.9, -59.33) * mm});
            skArc(sketch, "E311.MirrorCS", {"start": v(1.9, -59.33) * mm, "mid": v(2.61, -59.62) * mm, "end": v(2.9, -60.33) * mm});
            skLineSegment(sketch, "E312.MirrorCS", {"start": v(-1.9, -61.94) * mm, "end": v(1.9, -61.94) * mm});
            skArc(sketch, "E313.MirrorCS", {"start": v(-2.9, -60.94) * mm, "mid": v(-2.61, -61.65) * mm, "end": v(-1.9, -61.94) * mm});
            skArc(sketch, "E314.MirrorCS", {"start": v(1.9, -61.94) * mm, "mid": v(2.61, -61.65) * mm, "end": v(2.9, -60.94) * mm});
            skLineSegment(sketch, "E315.MirrorCS", {"start": v(2.9, -60.94) * mm, "end": v(2.9, -60.33) * mm});
            skLineSegment(sketch, "E316.MirrorCS", {"start": v(-2.9, -60.94) * mm, "end": v(-2.9, -60.33) * mm});
            skLineSegment(sketch, "E317", {"start": v(-1.25, -37.88) * mm, "end": v(-0.81, -37.1) * mm});
            skLineSegment(sketch, "E318.trimOffspring", {"start": v(0, -54.83) * mm, "end": v(0, -24.96) * mm, "construction": true});
            skLineSegment(sketch, "E319.MirrorCS", {"start": v(-1.25, -53.79) * mm, "end": v(-0.81, -54.58) * mm});
            skLineSegment(sketch, "E320.MirrorCS", {"start": v(1.25, -37.88) * mm, "end": v(0.81, -37.1) * mm});
            skArc(sketch, "E321", {"start": v(0.81, -37.1) * mm, "mid": v(0, -36.62) * mm, "end": v(-0.81, -37.1) * mm});
            skLineSegment(sketch, "E322.MirrorCS", {"start": v(1.25, -53.79) * mm, "end": v(0.81, -54.58) * mm});
            skArc(sketch, "E323.MirrorCS", {"start": v(0.81, -54.58) * mm, "mid": v(0, -55.05) * mm, "end": v(-0.81, -54.58) * mm});
            skLineSegment(sketch, "E324.MirrorCS", {"start": v(7.95, -44.59) * mm, "end": v(8.74, -45.02) * mm});
            skLineSegment(sketch, "E325.MirrorCS", {"start": v(7.95, -47.08) * mm, "end": v(8.74, -46.65) * mm});
            skArc(sketch, "E326.MirrorCS", {"start": v(8.74, -45.02) * mm, "mid": v(9.22, -45.84) * mm, "end": v(8.74, -46.65) * mm});
            skLineSegment(sketch, "E327.MirrorCS", {"start": v(-7.95, -44.59) * mm, "end": v(-8.74, -45.02) * mm});
            skLineSegment(sketch, "E328.MirrorCS", {"start": v(-7.95, -47.08) * mm, "end": v(-8.74, -46.65) * mm});
            skArc(sketch, "E329.MirrorCS", {"start": v(-8.74, -45.02) * mm, "mid": v(-9.22, -45.84) * mm, "end": v(-8.74, -46.65) * mm});
            skPoint(sketch, "E330.visualSharp", {"position": v(-11.83, -37.83) * mm});
            skPoint(sketch, "E331.endSnap0", {"position": v(-4.7, -50.54) * mm});
            skLineSegment(sketch, "E332", {"start": v(-12.02, -38.99) * mm, "end": v(-13.19, -49.45) * mm});
            skPoint(sketch, "E333.visualSharp", {"position": v(-8.74, -56.58) * mm});
            skArc(sketch, "E333.filletArc", {"start": v(-8.74, -57.34) * mm, "mid": v(-8.88, -56.63) * mm, "end": v(-9.25, -56) * mm});
            skArc(sketch, "E334.MirrorCS", {"start": v(8.74, -57.34) * mm, "mid": v(8.88, -56.63) * mm, "end": v(9.25, -56) * mm});
            skLineSegment(sketch, "E335.MirrorCS", {"start": v(8.74, -57.34) * mm, "end": v(8.74, -67.27) * mm});
            skLineSegment(sketch, "E336", {"start": v(-8.74, -67.27) * mm, "end": v(8.74, -67.27) * mm});
            skPoint(sketch, "E337.visualSharp", {"position": v(-4.92, -32.34) * mm});
            skPoint(sketch, "E338.visualSharp", {"position": v(-3.07, -28.95) * mm});
            skLineSegment(sketch, "E339", {"start": v(-6.4, -31.53) * mm, "end": v(-10.7, -36.12) * mm});
            skLineSegment(sketch, "E340", {"start": v(-9.25, -56) * mm, "end": v(-11.73, -53.56) * mm});
            skPoint(sketch, "E341.visualSharp", {"position": v(-13.45, -51.86) * mm});
            skArc(sketch, "E341.filletArc", {"start": v(-13.19, -49.45) * mm, "mid": v(-12.93, -51.68) * mm, "end": v(-11.73, -53.56) * mm});
            skPoint(sketch, "E342.visualSharp", {"position": v(-11.83, -37.34) * mm});
            skArc(sketch, "E342.filletArc", {"start": v(-10.7, -36.12) * mm, "mid": v(-11.6, -37.45) * mm, "end": v(-12.02, -38.99) * mm});
            skLineSegment(sketch, "E343.MirrorCS", {"start": v(6.4, -31.53) * mm, "end": v(10.7, -36.12) * mm});
            skArc(sketch, "E344.MirrorCS", {"start": v(10.7, -36.12) * mm, "mid": v(11.6, -37.45) * mm, "end": v(12.02, -38.99) * mm});
            skLineSegment(sketch, "E345.MirrorCS", {"start": v(12.02, -38.99) * mm, "end": v(13.19, -49.45) * mm});
            skArc(sketch, "E346.MirrorCS", {"start": v(13.19, -49.45) * mm, "mid": v(12.93, -51.68) * mm, "end": v(11.73, -53.56) * mm});
            skLineSegment(sketch, "E347.MirrorCS", {"start": v(9.25, -56) * mm, "end": v(11.73, -53.56) * mm});
            skPoint(sketch, "E348.visualSharp", {"position": v(3.2, -29.19) * mm});
            skArc(sketch, "E349", {"start": v(-6.4, -31.53) * mm, "mid": v(-4.77, -30.17) * mm, "end": v(-2.87, -29.24) * mm});
            skArc(sketch, "E350.trimOffspring", {"start": v(2.94, -29.27) * mm, "mid": v(4.8, -30.2) * mm, "end": v(6.4, -31.53) * mm});
            skPoint(sketch, "E351.visualSharp", {"position": v(-5.5, -41.17) * mm});
            skArc(sketch, "E352", {"start": v(-2.87, -29.24) * mm, "mid": v(0.03, -28.76) * mm, "end": v(2.94, -29.27) * mm});
            skCircle(sketch, "E353", {"center": v(-35.6, -40.59) * mm, "radius": 13.85 * mm, "construction": true});
            skLineSegment(sketch, "E354", {"start": v(-35.6, -40.59) * mm, "end": v(-24.3, -51.9) * mm, "construction": true});
            skArc(sketch, "E355", {"start": v(-29, -45.3) * mm, "mid": v(-30.9, -45.3) * mm, "end": v(-30.9, -47.2) * mm});
            skArc(sketch, "E356", {"start": v(-29.84, -48.26) * mm, "mid": v(-27.94, -48.26) * mm, "end": v(-27.94, -46.35) * mm});
            skLineSegment(sketch, "E357", {"start": v(-30.9, -47.2) * mm, "end": v(-29.84, -48.26) * mm});
            skLineSegment(sketch, "E358.MirrorCS", {"start": v(-29, -45.3) * mm, "end": v(-27.94, -46.35) * mm});
            skLineSegment(sketch, "E359.MirrorCS", {"start": v(-42.22, -45.3) * mm, "end": v(-43.28, -46.35) * mm});
            skArc(sketch, "E360.MirrorCS", {"start": v(-41.37, -48.26) * mm, "mid": v(-43.28, -48.26) * mm, "end": v(-43.28, -46.35) * mm});
            skLineSegment(sketch, "E361.MirrorCS", {"start": v(-40.3, -47.2) * mm, "end": v(-41.37, -48.26) * mm});
            skArc(sketch, "E362.MirrorCS", {"start": v(-42.22, -45.3) * mm, "mid": v(-40.3, -45.3) * mm, "end": v(-40.3, -47.2) * mm});
            skLineSegment(sketch, "E363.MirrorCS", {"start": v(-40.3, -33.98) * mm, "end": v(-41.37, -32.92) * mm});
            skLineSegment(sketch, "E364.MirrorCS", {"start": v(-42.22, -35.89) * mm, "end": v(-43.28, -34.83) * mm});
            skArc(sketch, "E365.MirrorCS", {"start": v(-42.22, -35.89) * mm, "mid": v(-40.3, -35.89) * mm, "end": v(-40.3, -33.98) * mm});
            skArc(sketch, "E366.MirrorCS", {"start": v(-41.37, -32.92) * mm, "mid": v(-43.28, -32.92) * mm, "end": v(-43.28, -34.83) * mm});
            skLineSegment(sketch, "E367.MirrorCS", {"start": v(-30.9, -33.98) * mm, "end": v(-29.84, -32.92) * mm});
            skLineSegment(sketch, "E368.MirrorCS", {"start": v(-29, -35.89) * mm, "end": v(-27.94, -34.83) * mm});
            skArc(sketch, "E369.MirrorCS", {"start": v(-29.84, -32.92) * mm, "mid": v(-27.94, -32.92) * mm, "end": v(-27.94, -34.83) * mm});
            skArc(sketch, "E370.MirrorCS", {"start": v(-29, -35.89) * mm, "mid": v(-30.9, -35.89) * mm, "end": v(-30.9, -33.98) * mm});
            skLineSegment(sketch, "E371", {"start": v(-32.67, -26.35) * mm, "end": v(-32.67, -26.96) * mm});
            skLineSegment(sketch, "E372", {"start": v(-38.48, -26.35) * mm, "end": v(-38.48, -26.96) * mm});
            skArc(sketch, "E373", {"start": v(-34.1, -44.3) * mm, "mid": v(-32.78, -43.42) * mm, "end": v(-31.9, -42.09) * mm});
            skLineSegment(sketch, "E374.bottom", {"start": v(-42.59, -39.09) * mm, "end": v(-39.32, -39.09) * mm});
            skLineSegment(sketch, "E374.top", {"start": v(-42.59, -42.09) * mm, "end": v(-39.32, -42.09) * mm});
            skLineSegment(sketch, "E375.left", {"start": v(-37.1, -33.6) * mm, "end": v(-37.1, -36.88) * mm});
            skLineSegment(sketch, "E375.right", {"start": v(-34.1, -33.6) * mm, "end": v(-34.1, -36.88) * mm});
            skLineSegment(sketch, "E376.trimOffspring", {"start": v(-31.9, -42.09) * mm, "end": v(-28.62, -42.09) * mm});
            skLineSegment(sketch, "E377.trimOffspring", {"start": v(-31.9, -39.09) * mm, "end": v(-28.62, -39.09) * mm});
            skLineSegment(sketch, "E378.trimOffspring", {"start": v(-34.1, -44.3) * mm, "end": v(-34.1, -47.57) * mm});
            skLineSegment(sketch, "E379.trimOffspring", {"start": v(-37.1, -44.3) * mm, "end": v(-37.1, -47.57) * mm});
            skArc(sketch, "E380.trimOffspring", {"start": v(-31.9, -39.09) * mm, "mid": v(-32.78, -37.76) * mm, "end": v(-34.1, -36.88) * mm});
            skArc(sketch, "E381.trimOffspring", {"start": v(-37.1, -36.88) * mm, "mid": v(-38.44, -37.76) * mm, "end": v(-39.32, -39.09) * mm});
            skArc(sketch, "E382.trimOffspring", {"start": v(-39.32, -42.09) * mm, "mid": v(-38.44, -43.42) * mm, "end": v(-37.1, -44.3) * mm});
            skArc(sketch, "E383", {"start": v(-26.33, -41.1) * mm, "mid": v(-26.28, -41.07) * mm, "end": v(-26.23, -41.03) * mm});
            skArc(sketch, "E384.filletArc", {"start": v(-28.62, -42.09) * mm, "mid": v(-28.12, -42.03) * mm, "end": v(-27.65, -41.84) * mm});
            skArc(sketch, "E385.filletArc", {"start": v(-27.65, -39.34) * mm, "mid": v(-28.12, -39.15) * mm, "end": v(-28.62, -39.09) * mm});
            skArc(sketch, "E386.MirrorCS", {"start": v(-43.56, -39.34) * mm, "mid": v(-43.1, -39.15) * mm, "end": v(-42.59, -39.09) * mm});
            skArc(sketch, "E387.MirrorCS", {"start": v(-42.59, -42.09) * mm, "mid": v(-43.1, -42.03) * mm, "end": v(-43.56, -41.84) * mm});
            skArc(sketch, "E388.MirrorCS", {"start": v(-44.88, -41.1) * mm, "mid": v(-44.94, -41.07) * mm, "end": v(-44.99, -41.03) * mm});
            skArc(sketch, "E389.MirrorCS", {"start": v(-34.36, -48.54) * mm, "mid": v(-34.17, -48.07) * mm, "end": v(-34.1, -47.57) * mm});
            skArc(sketch, "E390.MirrorCS", {"start": v(-37.1, -47.57) * mm, "mid": v(-37.04, -48.07) * mm, "end": v(-36.86, -48.54) * mm});
            skArc(sketch, "E391.MirrorCS", {"start": v(-37.1, -33.6) * mm, "mid": v(-37.04, -33.1) * mm, "end": v(-36.86, -32.64) * mm});
            skArc(sketch, "E392.MirrorCS", {"start": v(-34.36, -32.64) * mm, "mid": v(-34.17, -33.1) * mm, "end": v(-34.1, -33.6) * mm});
            skArc(sketch, "E393.filletArc", {"start": v(-33.67, -27.96) * mm, "mid": v(-32.96, -27.66) * mm, "end": v(-32.67, -26.96) * mm});
            skArc(sketch, "E394.filletArc", {"start": v(-38.48, -26.96) * mm, "mid": v(-38.19, -27.66) * mm, "end": v(-37.48, -27.96) * mm});
            skCircle(sketch, "E395", {"center": v(-35.6, -40.59) * mm, "radius": 8 * mm, "construction": true});
            skLineSegment(sketch, "E396.MirrorCS", {"start": v(-44.35, -52.1) * mm, "end": v(-44.35, -62.02) * mm});
            skLineSegment(sketch, "E397", {"start": v(-37.48, -27.96) * mm, "end": v(-33.67, -27.96) * mm});
            skLineSegment(sketch, "E398.MirrorCS", {"start": v(-37.51, -54.08) * mm, "end": v(-33.7, -54.08) * mm});
            skArc(sketch, "E399.MirrorCS", {"start": v(-38.51, -55.08) * mm, "mid": v(-38.22, -54.37) * mm, "end": v(-37.51, -54.08) * mm});
            skArc(sketch, "E400.MirrorCS", {"start": v(-33.7, -54.08) * mm, "mid": v(-33, -54.37) * mm, "end": v(-32.7, -55.08) * mm});
            skLineSegment(sketch, "E401.MirrorCS", {"start": v(-37.51, -56.7) * mm, "end": v(-33.7, -56.7) * mm});
            skArc(sketch, "E402.MirrorCS", {"start": v(-38.51, -55.7) * mm, "mid": v(-38.22, -56.4) * mm, "end": v(-37.51, -56.7) * mm});
            skArc(sketch, "E403.MirrorCS", {"start": v(-33.7, -56.7) * mm, "mid": v(-33, -56.4) * mm, "end": v(-32.7, -55.7) * mm});
            skLineSegment(sketch, "E404.MirrorCS", {"start": v(-32.7, -55.7) * mm, "end": v(-32.7, -55.08) * mm});
            skLineSegment(sketch, "E405.MirrorCS", {"start": v(-38.51, -55.7) * mm, "end": v(-38.51, -55.08) * mm});
            skLineSegment(sketch, "E406", {"start": v(-36.86, -32.64) * mm, "end": v(-36.42, -31.85) * mm});
            skLineSegment(sketch, "E407.trimOffspring", {"start": v(-22.6, -47.88) * mm, "end": v(-22.6, -18.02) * mm, "construction": true});
            skLineSegment(sketch, "E408.MirrorCS", {"start": v(-36.86, -48.54) * mm, "end": v(-36.42, -49.33) * mm});
            skLineSegment(sketch, "E409.MirrorCS", {"start": v(-34.36, -32.64) * mm, "end": v(-34.8, -31.85) * mm});
            skArc(sketch, "E410", {"start": v(-34.8, -31.85) * mm, "mid": v(-35.6, -31.37) * mm, "end": v(-36.42, -31.85) * mm});
            skLineSegment(sketch, "E411.MirrorCS", {"start": v(-34.36, -48.54) * mm, "end": v(-34.8, -49.33) * mm});
            skArc(sketch, "E412.MirrorCS", {"start": v(-34.8, -49.33) * mm, "mid": v(-35.6, -49.8) * mm, "end": v(-36.42, -49.33) * mm});
            skLineSegment(sketch, "E413.MirrorCS", {"start": v(-27.65, -39.34) * mm, "end": v(-26.87, -39.78) * mm});
            skLineSegment(sketch, "E414.MirrorCS", {"start": v(-27.65, -41.84) * mm, "end": v(-26.87, -41.4) * mm});
            skArc(sketch, "E415.MirrorCS", {"start": v(-26.87, -39.78) * mm, "mid": v(-26.39, -40.59) * mm, "end": v(-26.87, -41.4) * mm});
            skLineSegment(sketch, "E416.MirrorCS", {"start": v(-43.56, -39.34) * mm, "end": v(-44.35, -39.78) * mm});
            skLineSegment(sketch, "E417.MirrorCS", {"start": v(-43.56, -41.84) * mm, "end": v(-44.35, -41.4) * mm});
            skArc(sketch, "E418.MirrorCS", {"start": v(-44.35, -39.78) * mm, "mid": v(-44.83, -40.59) * mm, "end": v(-44.35, -41.4) * mm});
            skPoint(sketch, "E419.visualSharp", {"position": v(-47.44, -32.58) * mm});
            skPoint(sketch, "E420.endSnap0", {"position": v(-40.3, -45.3) * mm});
            skLineSegment(sketch, "E421", {"start": v(-47.63, -33.74) * mm, "end": v(-48.8, -44.2) * mm});
            skPoint(sketch, "E422.visualSharp", {"position": v(-44.35, -51.33) * mm});
            skArc(sketch, "E422.filletArc", {"start": v(-44.35, -52.1) * mm, "mid": v(-44.48, -51.38) * mm, "end": v(-44.86, -50.76) * mm});
            skArc(sketch, "E423.MirrorCS", {"start": v(-26.86, -52.1) * mm, "mid": v(-26.73, -51.38) * mm, "end": v(-26.35, -50.76) * mm});
            skLineSegment(sketch, "E424.MirrorCS", {"start": v(-26.86, -52.1) * mm, "end": v(-26.86, -62.02) * mm});
            skLineSegment(sketch, "E425", {"start": v(-44.35, -62.02) * mm, "end": v(-26.86, -62.02) * mm});
            skPoint(sketch, "E426.visualSharp", {"position": v(-40.53, -27.09) * mm});
            skPoint(sketch, "E427.visualSharp", {"position": v(-38.68, -23.7) * mm});
            skLineSegment(sketch, "E428", {"start": v(-44.86, -50.76) * mm, "end": v(-47.34, -48.32) * mm});
            skPoint(sketch, "E429.visualSharp", {"position": v(-49.06, -46.61) * mm});
            skArc(sketch, "E429.filletArc", {"start": v(-48.8, -44.2) * mm, "mid": v(-48.54, -46.43) * mm, "end": v(-47.34, -48.32) * mm});
            skPoint(sketch, "E430.visualSharp", {"position": v(-47.44, -32.1) * mm});
            skArc(sketch, "E430.filletArc", {"start": v(-46.3, -30.88) * mm, "mid": v(-47.2, -32.2) * mm, "end": v(-47.63, -33.74) * mm});
            skArc(sketch, "E431.MirrorCS", {"start": v(-24.9, -30.88) * mm, "mid": v(-24.02, -32.2) * mm, "end": v(-23.59, -33.74) * mm});
            skLineSegment(sketch, "E432.MirrorCS", {"start": v(-23.59, -33.74) * mm, "end": v(-22.42, -44.2) * mm});
            skArc(sketch, "E433.MirrorCS", {"start": v(-22.42, -44.2) * mm, "mid": v(-22.68, -46.43) * mm, "end": v(-23.88, -48.32) * mm});
            skLineSegment(sketch, "E434.MirrorCS", {"start": v(-26.35, -50.76) * mm, "end": v(-23.88, -48.32) * mm});
            skPoint(sketch, "E435.visualSharp", {"position": v(-32.4, -23.94) * mm});
            skPoint(sketch, "E436.visualSharp", {"position": v(-17.96, -46.51) * mm});
            skLineSegment(sketch, "E437", {"start": v(-46.3, -30.88) * mm, "end": v(-38.68, -24.93) * mm});
            skLineSegment(sketch, "E438", {"start": v(-35.6, -40.59) * mm, "end": v(-35.6, -16.3) * mm, "construction": true});
            skPoint(sketch, "E439.MirrorP", {"position": v(-30.69, -27.09) * mm});
            skLineSegment(sketch, "E440.MirrorCS", {"start": v(-24.9, -30.88) * mm, "end": v(-32.54, -24.93) * mm});
            skArc(sketch, "E441", {"start": v(-38.68, -24.93) * mm, "mid": v(-35.6, -23.87) * mm, "end": v(-32.54, -24.93) * mm});
            skLineSegment(sketch, "E442", {"start": v(-35.6, -25.65) * mm, "end": v(-37.54, -25.65) * mm});
            skLineSegment(sketch, "E443.MirrorCS", {"start": v(-35.6, -25.65) * mm, "end": v(-33.68, -25.65) * mm});
            skArc(sketch, "E444", {"start": v(-37.54, -25.65) * mm, "mid": v(-38.12, -25.84) * mm, "end": v(-38.48, -26.35) * mm});
            skArc(sketch, "E445", {"start": v(-33.68, -25.65) * mm, "mid": v(-33.06, -25.84) * mm, "end": v(-32.67, -26.35) * mm});
            skLineSegment(sketch, "E446", {"start": v(-78.35, -40.74) * mm, "end": v(-67.04, -52.06) * mm, "construction": true});
            skArc(sketch, "E447", {"start": v(-71.74, -45.45) * mm, "mid": v(-73.65, -45.45) * mm, "end": v(-73.65, -47.36) * mm});
            skArc(sketch, "E448", {"start": v(-72.47, -48.53) * mm, "mid": v(-70.56, -48.53) * mm, "end": v(-70.56, -46.63) * mm});
            skLineSegment(sketch, "E449", {"start": v(-73.65, -47.36) * mm, "end": v(-72.47, -48.53) * mm});
            skLineSegment(sketch, "E450.MirrorCS", {"start": v(-71.74, -45.45) * mm, "end": v(-70.56, -46.63) * mm});
            skLineSegment(sketch, "E451.MirrorCS", {"start": v(-84.96, -45.45) * mm, "end": v(-86.02, -46.5) * mm});
            skArc(sketch, "E452.MirrorCS", {"start": v(-84.11, -48.42) * mm, "mid": v(-86.02, -48.42) * mm, "end": v(-86.02, -46.5) * mm});
            skLineSegment(sketch, "E453.MirrorCS", {"start": v(-83.05, -47.36) * mm, "end": v(-84.11, -48.42) * mm});
            skArc(sketch, "E454.MirrorCS", {"start": v(-84.96, -45.45) * mm, "mid": v(-83.05, -45.45) * mm, "end": v(-83.05, -47.36) * mm});
            skLineSegment(sketch, "E455.MirrorCS", {"start": v(-83.04, -34.1) * mm, "end": v(-84, -33.2) * mm});
            skLineSegment(sketch, "E456.MirrorCS", {"start": v(-84.85, -36.17) * mm, "end": v(-85.92, -35.11) * mm});
            skArc(sketch, "E457.MirrorCS", {"start": v(-84.85, -36.17) * mm, "mid": v(-82.98, -36) * mm, "end": v(-83.04, -34.1) * mm});
            skArc(sketch, "E458.MirrorCS", {"start": v(-84, -33.2) * mm, "mid": v(-85.92, -33.2) * mm, "end": v(-85.92, -35.11) * mm});
            skLineSegment(sketch, "E459.MirrorCS", {"start": v(-73.65, -34.13) * mm, "end": v(-72.59, -33.07) * mm});
            skLineSegment(sketch, "E460.MirrorCS", {"start": v(-71.74, -36.04) * mm, "end": v(-70.68, -34.98) * mm});
            skArc(sketch, "E461.MirrorCS", {"start": v(-72.59, -33.07) * mm, "mid": v(-70.68, -33.07) * mm, "end": v(-70.68, -34.98) * mm});
            skArc(sketch, "E462.MirrorCS", {"start": v(-71.74, -36.04) * mm, "mid": v(-73.65, -36.04) * mm, "end": v(-73.65, -34.13) * mm});
            skLineSegment(sketch, "E463", {"start": v(-75.42, -26.5) * mm, "end": v(-75.42, -27.11) * mm});
            skLineSegment(sketch, "E464", {"start": v(-81.22, -26.5) * mm, "end": v(-81.22, -27.11) * mm});
            skArc(sketch, "E465", {"start": v(-76.85, -44.45) * mm, "mid": v(-75.52, -43.57) * mm, "end": v(-74.64, -42.24) * mm});
            skLineSegment(sketch, "E466.bottom", {"start": v(-85.33, -39.24) * mm, "end": v(-82.06, -39.24) * mm});
            skLineSegment(sketch, "E466.top", {"start": v(-85.33, -42.24) * mm, "end": v(-82.06, -42.24) * mm});
            skLineSegment(sketch, "E467.left", {"start": v(-79.85, -33.76) * mm, "end": v(-79.85, -37.04) * mm});
            skLineSegment(sketch, "E467.right", {"start": v(-76.85, -33.76) * mm, "end": v(-76.85, -37.04) * mm});
            skLineSegment(sketch, "E468.trimOffspring", {"start": v(-74.64, -42.24) * mm, "end": v(-71.37, -42.24) * mm});
            skLineSegment(sketch, "E469.trimOffspring", {"start": v(-74.64, -39.24) * mm, "end": v(-71.37, -39.24) * mm});
            skLineSegment(sketch, "E470.trimOffspring", {"start": v(-76.85, -44.45) * mm, "end": v(-76.85, -47.73) * mm});
            skLineSegment(sketch, "E471.trimOffspring", {"start": v(-79.85, -44.45) * mm, "end": v(-79.85, -47.73) * mm});
            skArc(sketch, "E472.trimOffspring", {"start": v(-74.64, -39.24) * mm, "mid": v(-75.52, -37.92) * mm, "end": v(-76.85, -37.04) * mm});
            skArc(sketch, "E473.trimOffspring", {"start": v(-79.85, -37.04) * mm, "mid": v(-81.18, -37.92) * mm, "end": v(-82.06, -39.24) * mm});
            skArc(sketch, "E474.trimOffspring", {"start": v(-82.06, -42.24) * mm, "mid": v(-81.18, -43.57) * mm, "end": v(-79.85, -44.45) * mm});
            skArc(sketch, "E475", {"start": v(-69.08, -41.26) * mm, "mid": v(-69.02, -41.22) * mm, "end": v(-68.97, -41.18) * mm});
            skArc(sketch, "E476.filletArc", {"start": v(-71.37, -42.24) * mm, "mid": v(-70.87, -42.18) * mm, "end": v(-70.4, -42) * mm});
            skArc(sketch, "E477.filletArc", {"start": v(-70.4, -39.5) * mm, "mid": v(-70.87, -39.3) * mm, "end": v(-71.37, -39.24) * mm});
            skArc(sketch, "E478.MirrorCS", {"start": v(-86.3, -39.5) * mm, "mid": v(-85.84, -39.3) * mm, "end": v(-85.33, -39.24) * mm});
            skArc(sketch, "E479.MirrorCS", {"start": v(-85.33, -42.24) * mm, "mid": v(-85.84, -42.18) * mm, "end": v(-86.3, -42) * mm});
            skArc(sketch, "E480.MirrorCS", {"start": v(-87.63, -41.26) * mm, "mid": v(-87.68, -41.22) * mm, "end": v(-87.73, -41.18) * mm});
            skArc(sketch, "E481.MirrorCS", {"start": v(-77.1, -48.7) * mm, "mid": v(-76.92, -48.23) * mm, "end": v(-76.85, -47.73) * mm});
            skArc(sketch, "E482.MirrorCS", {"start": v(-79.85, -47.73) * mm, "mid": v(-79.79, -48.23) * mm, "end": v(-79.6, -48.7) * mm});
            skArc(sketch, "E483.MirrorCS", {"start": v(-79.85, -33.76) * mm, "mid": v(-79.79, -33.26) * mm, "end": v(-79.6, -32.8) * mm});
            skArc(sketch, "E484.MirrorCS", {"start": v(-77.1, -32.8) * mm, "mid": v(-76.92, -33.26) * mm, "end": v(-76.85, -33.76) * mm});
            skArc(sketch, "E485.filletArc", {"start": v(-76.42, -28.11) * mm, "mid": v(-75.7, -27.82) * mm, "end": v(-75.42, -27.11) * mm});
            skArc(sketch, "E486.filletArc", {"start": v(-81.22, -27.11) * mm, "mid": v(-80.93, -27.82) * mm, "end": v(-80.22, -28.11) * mm});
            skCircle(sketch, "E487", {"center": v(-78.35, -40.74) * mm, "radius": 8 * mm, "construction": true});
            skLineSegment(sketch, "E488.MirrorCS", {"start": v(-87.1, -52.25) * mm, "end": v(-87.1, -62.18) * mm});
            skLineSegment(sketch, "E489", {"start": v(-80.22, -28.11) * mm, "end": v(-76.42, -28.11) * mm});
            skLineSegment(sketch, "E490.MirrorCS", {"start": v(-80.26, -54.23) * mm, "end": v(-76.45, -54.23) * mm});
            skArc(sketch, "E491.MirrorCS", {"start": v(-81.26, -55.23) * mm, "mid": v(-80.96, -54.53) * mm, "end": v(-80.26, -54.23) * mm});
            skArc(sketch, "E492.MirrorCS", {"start": v(-76.45, -54.23) * mm, "mid": v(-75.74, -54.53) * mm, "end": v(-75.45, -55.23) * mm});
            skLineSegment(sketch, "E493.MirrorCS", {"start": v(-80.26, -56.85) * mm, "end": v(-76.45, -56.85) * mm});
            skArc(sketch, "E494.MirrorCS", {"start": v(-81.26, -55.85) * mm, "mid": v(-80.96, -56.55) * mm, "end": v(-80.26, -56.85) * mm});
            skArc(sketch, "E495.MirrorCS", {"start": v(-76.45, -56.85) * mm, "mid": v(-75.74, -56.55) * mm, "end": v(-75.45, -55.85) * mm});
            skLineSegment(sketch, "E496.MirrorCS", {"start": v(-75.45, -55.85) * mm, "end": v(-75.45, -55.23) * mm});
            skLineSegment(sketch, "E497.MirrorCS", {"start": v(-81.26, -55.85) * mm, "end": v(-81.26, -55.23) * mm});
            skLineSegment(sketch, "E498", {"start": v(-79.6, -32.8) * mm, "end": v(-79.16, -32) * mm});
            skLineSegment(sketch, "E499.trimOffspring", {"start": v(-65.35, -48.03) * mm, "end": v(-65.35, -18.17) * mm, "construction": true});
            skLineSegment(sketch, "E500.MirrorCS", {"start": v(-79.6, -48.7) * mm, "end": v(-79.16, -49.48) * mm});
            skLineSegment(sketch, "E501.MirrorCS", {"start": v(-77.1, -32.8) * mm, "end": v(-77.54, -32) * mm});
            skArc(sketch, "E502", {"start": v(-77.54, -32) * mm, "mid": v(-78.35, -31.53) * mm, "end": v(-79.16, -32) * mm});
            skLineSegment(sketch, "E503.MirrorCS", {"start": v(-77.1, -48.7) * mm, "end": v(-77.54, -49.48) * mm});
            skArc(sketch, "E504.MirrorCS", {"start": v(-77.54, -49.48) * mm, "mid": v(-78.35, -49.96) * mm, "end": v(-79.16, -49.48) * mm});
            skLineSegment(sketch, "E505.MirrorCS", {"start": v(-70.4, -39.5) * mm, "end": v(-69.61, -39.93) * mm});
            skLineSegment(sketch, "E506.MirrorCS", {"start": v(-70.4, -42) * mm, "end": v(-69.61, -41.56) * mm});
            skArc(sketch, "E507.MirrorCS", {"start": v(-69.61, -39.93) * mm, "mid": v(-69.13, -40.74) * mm, "end": v(-69.61, -41.56) * mm});
            skLineSegment(sketch, "E508.MirrorCS", {"start": v(-86.3, -39.5) * mm, "end": v(-87.1, -39.93) * mm});
            skLineSegment(sketch, "E509.MirrorCS", {"start": v(-86.3, -42) * mm, "end": v(-87.1, -41.56) * mm});
            skArc(sketch, "E510.MirrorCS", {"start": v(-87.1, -39.93) * mm, "mid": v(-87.57, -40.74) * mm, "end": v(-87.1, -41.56) * mm});
            skPoint(sketch, "E511.visualSharp", {"position": v(-90.19, -32.74) * mm});
            skPoint(sketch, "E512.endSnap0", {"position": v(-83.05, -45.45) * mm});
            skLineSegment(sketch, "E513", {"start": v(-90.37, -33.9) * mm, "end": v(-91.54, -44.36) * mm});
            skPoint(sketch, "E514.visualSharp", {"position": v(-87.1, -51.48) * mm});
            skLineSegment(sketch, "E515.MirrorCS", {"start": v(-69.6, -52.25) * mm, "end": v(-69.6, -62.18) * mm});
            skLineSegment(sketch, "E516", {"start": v(-87.1, -62.18) * mm, "end": v(-69.6, -62.18) * mm});
            skPoint(sketch, "E517.visualSharp", {"position": v(-83.27, -27.24) * mm});
            skPoint(sketch, "E518.visualSharp", {"position": v(-81.42, -23.86) * mm});
            skPoint(sketch, "E519.visualSharp", {"position": v(-91.8, -46.77) * mm});
            skArc(sketch, "E519.filletArc", {"start": v(-91.54, -44.36) * mm, "mid": v(-91.56, -44.62) * mm, "end": v(-91.57, -44.89) * mm});
            skPoint(sketch, "E520.visualSharp", {"position": v(-90.19, -32.24) * mm});
            skArc(sketch, "E520.filletArc", {"start": v(-89.05, -31.03) * mm, "mid": v(-89.94, -32.36) * mm, "end": v(-90.37, -33.9) * mm});
            skArc(sketch, "E521.MirrorCS", {"start": v(-66.34, -33.85) * mm, "mid": v(-66.34, -33.87) * mm, "end": v(-66.33, -33.9) * mm});
            skPoint(sketch, "E522.visualSharp", {"position": v(-75.15, -24.1) * mm});
            skPoint(sketch, "E523.MirrorP", {"position": v(-73.43, -27.24) * mm});
            skArc(sketch, "E524", {"start": v(-81.42, -25.08) * mm, "mid": v(-78.35, -24.03) * mm, "end": v(-75.28, -25.08) * mm});
            skLineSegment(sketch, "E525", {"start": v(-78.35, -25.8) * mm, "end": v(-80.28, -25.8) * mm});
            skLineSegment(sketch, "E526.MirrorCS", {"start": v(-78.35, -25.8) * mm, "end": v(-76.42, -25.8) * mm});
            skArc(sketch, "E527", {"start": v(-80.28, -25.8) * mm, "mid": v(-80.87, -26) * mm, "end": v(-81.22, -26.5) * mm});
            skArc(sketch, "E528", {"start": v(-76.42, -25.8) * mm, "mid": v(-75.8, -26) * mm, "end": v(-75.42, -26.5) * mm});
            skFitSpline(sketch, "E529", {"points": [v(-81.42, -25.08) * mm, v(-89.05, -31.03) * mm], "startDerivative": vector(-13.54, -12.22) * mm, "endDerivative": vector(-7.28, -8.12) * mm});
            skFitSpline(sketch, "E530", {"points": [v(-91.57, -44.89) * mm, v(-87.1, -52.25) * mm], "startDerivative": vector(-0.41, -9.73) * mm, "endDerivative": vector(2.65, -9.88) * mm});
            skLineSegment(sketch, "E531", {"start": v(-78.35, -40.74) * mm, "end": v(-78.35, -46.43) * mm, "construction": true});
            skLineSegment(sketch, "E532.MirrorCS", {"start": v(-66.33, -33.9) * mm, "end": v(-65.17, -44.36) * mm});
            skFitSpline(sketch, "E533.MirrorCS", {"points": [v(-75.28, -25.08) * mm, v(-67.65, -31.03) * mm], "startDerivative": vector(13.54, -12.22) * mm, "endDerivative": vector(7.28, -8.12) * mm});
            skArc(sketch, "E534.MirrorCS", {"start": v(-67.65, -31.03) * mm, "mid": v(-66.76, -32.36) * mm, "end": v(-66.33, -33.9) * mm});
            skLineSegment(sketch, "E535", {"start": v(-65.17, -44.36) * mm, "end": v(-65.14, -44.89) * mm});
            skCircle(sketch, "E536", {"center": v(-78.35, -40.74) * mm, "radius": 14.15 * mm, "construction": true});
            skFitSpline(sketch, "E537.MirrorCS", {"points": [v(-65.14, -44.89) * mm, v(-69.6, -52.25) * mm], "startDerivative": vector(0.41, -9.73) * mm, "endDerivative": vector(-2.65, -9.88) * mm});
            skSolve(sketch);
        }
        {
            var Q0;
            Q0=qCreatedBy(makeId("Top.planeOp"),FACE);
            var sketch = newSketch(context, id + "F4", { "sketchPlane" : qUnion([Q0])});
            skCircle(sketch, "E538", {"center": v(32.08, -46) * mm, "radius": 13.85 * mm, "construction": true});
            skLineSegment(sketch, "E539", {"start": v(32.08, -46) * mm, "end": v(43.4, -57.31) * mm, "construction": true});
            skArc(sketch, "E540", {"start": v(38.7, -50.7) * mm, "mid": v(36.79, -50.7) * mm, "end": v(36.79, -52.6) * mm});
            skArc(sketch, "E541", {"start": v(37.85, -53.67) * mm, "mid": v(39.76, -53.67) * mm, "end": v(39.76, -51.76) * mm});
            skLineSegment(sketch, "E542", {"start": v(36.79, -52.6) * mm, "end": v(37.85, -53.67) * mm});
            skLineSegment(sketch, "E543.MirrorCS", {"start": v(38.7, -50.7) * mm, "end": v(39.76, -51.76) * mm});
            skLineSegment(sketch, "E544.MirrorCS", {"start": v(25.47, -50.7) * mm, "end": v(24.41, -51.76) * mm});
            skArc(sketch, "E545.MirrorCS", {"start": v(26.32, -53.67) * mm, "mid": v(24.41, -53.67) * mm, "end": v(24.41, -51.76) * mm});
            skLineSegment(sketch, "E546.MirrorCS", {"start": v(27.38, -52.6) * mm, "end": v(26.32, -53.67) * mm});
            skArc(sketch, "E547.MirrorCS", {"start": v(25.47, -50.7) * mm, "mid": v(27.38, -50.7) * mm, "end": v(27.38, -52.6) * mm});
            skLineSegment(sketch, "E548.MirrorCS", {"start": v(27.38, -39.39) * mm, "end": v(26.32, -38.33) * mm});
            skLineSegment(sketch, "E549.MirrorCS", {"start": v(25.47, -41.3) * mm, "end": v(24.41, -40.24) * mm});
            skArc(sketch, "E550.MirrorCS", {"start": v(25.47, -41.3) * mm, "mid": v(27.38, -41.3) * mm, "end": v(27.38, -39.39) * mm});
            skArc(sketch, "E551.MirrorCS", {"start": v(26.32, -38.33) * mm, "mid": v(24.41, -38.33) * mm, "end": v(24.41, -40.24) * mm});
            skLineSegment(sketch, "E552.MirrorCS", {"start": v(36.79, -39.39) * mm, "end": v(37.85, -38.33) * mm});
            skLineSegment(sketch, "E553.MirrorCS", {"start": v(38.7, -41.3) * mm, "end": v(39.76, -40.24) * mm});
            skArc(sketch, "E554.MirrorCS", {"start": v(37.85, -38.33) * mm, "mid": v(39.76, -38.33) * mm, "end": v(39.76, -40.24) * mm});
            skArc(sketch, "E555.MirrorCS", {"start": v(38.7, -41.3) * mm, "mid": v(36.79, -41.3) * mm, "end": v(36.79, -39.39) * mm});
            skLineSegment(sketch, "E556", {"start": v(35.02, -31.75) * mm, "end": v(35.02, -32.37) * mm});
            skLineSegment(sketch, "E557", {"start": v(29.21, -31.75) * mm, "end": v(29.21, -32.37) * mm});
            skArc(sketch, "E558", {"start": v(33.58, -49.7) * mm, "mid": v(34.91, -48.83) * mm, "end": v(35.8, -47.5) * mm});
            skLineSegment(sketch, "E559.bottom", {"start": v(25.1, -44.5) * mm, "end": v(28.38, -44.5) * mm});
            skLineSegment(sketch, "E559.top", {"start": v(25.1, -47.5) * mm, "end": v(28.38, -47.5) * mm});
            skLineSegment(sketch, "E560.left", {"start": v(30.58, -39.02) * mm, "end": v(30.58, -42.3) * mm});
            skLineSegment(sketch, "E560.right", {"start": v(33.58, -39.02) * mm, "end": v(33.58, -42.3) * mm});
            skLineSegment(sketch, "E561.trimOffspring", {"start": v(35.8, -47.5) * mm, "end": v(39.07, -47.5) * mm});
            skLineSegment(sketch, "E562.trimOffspring", {"start": v(35.8, -44.5) * mm, "end": v(39.07, -44.5) * mm});
            skLineSegment(sketch, "E563.trimOffspring", {"start": v(33.58, -49.7) * mm, "end": v(33.58, -52.98) * mm});
            skLineSegment(sketch, "E564.trimOffspring", {"start": v(30.58, -49.7) * mm, "end": v(30.58, -52.98) * mm});
            skArc(sketch, "E565.trimOffspring", {"start": v(35.8, -44.5) * mm, "mid": v(34.91, -43.17) * mm, "end": v(33.58, -42.3) * mm});
            skArc(sketch, "E566.trimOffspring", {"start": v(30.58, -42.3) * mm, "mid": v(29.26, -43.17) * mm, "end": v(28.38, -44.5) * mm});
            skArc(sketch, "E567.trimOffspring", {"start": v(28.38, -47.5) * mm, "mid": v(29.26, -48.83) * mm, "end": v(30.58, -49.7) * mm});
            skArc(sketch, "E568", {"start": v(41.36, -46.51) * mm, "mid": v(41.42, -46.48) * mm, "end": v(41.47, -46.44) * mm});
            skArc(sketch, "E569.filletArc", {"start": v(39.07, -47.5) * mm, "mid": v(39.57, -47.43) * mm, "end": v(40.04, -47.25) * mm});
            skArc(sketch, "E570.filletArc", {"start": v(40.04, -44.75) * mm, "mid": v(39.57, -44.56) * mm, "end": v(39.07, -44.5) * mm});
            skArc(sketch, "E571.MirrorCS", {"start": v(24.13, -44.75) * mm, "mid": v(24.6, -44.56) * mm, "end": v(25.1, -44.5) * mm});
            skArc(sketch, "E572.MirrorCS", {"start": v(25.1, -47.5) * mm, "mid": v(24.6, -47.43) * mm, "end": v(24.13, -47.25) * mm});
            skArc(sketch, "E573.MirrorCS", {"start": v(22.8, -46.51) * mm, "mid": v(22.75, -46.48) * mm, "end": v(22.7, -46.44) * mm});
            skArc(sketch, "E574.MirrorCS", {"start": v(33.33, -53.95) * mm, "mid": v(33.52, -53.48) * mm, "end": v(33.58, -52.98) * mm});
            skArc(sketch, "E575.MirrorCS", {"start": v(30.58, -52.98) * mm, "mid": v(30.65, -53.48) * mm, "end": v(30.84, -53.95) * mm});
            skArc(sketch, "E576.MirrorCS", {"start": v(30.58, -39.02) * mm, "mid": v(30.65, -38.51) * mm, "end": v(30.84, -38.05) * mm});
            skArc(sketch, "E577.MirrorCS", {"start": v(33.33, -38.05) * mm, "mid": v(33.52, -38.51) * mm, "end": v(33.58, -39.02) * mm});
            skArc(sketch, "E578.filletArc", {"start": v(34.02, -33.37) * mm, "mid": v(34.73, -33.07) * mm, "end": v(35.02, -32.37) * mm});
            skArc(sketch, "E579.filletArc", {"start": v(29.21, -32.37) * mm, "mid": v(29.5, -33.07) * mm, "end": v(30.21, -33.37) * mm});
            skCircle(sketch, "E580", {"center": v(32.08, -46) * mm, "radius": 8 * mm, "construction": true});
            skLineSegment(sketch, "E581.MirrorCS", {"start": v(23.34, -57.5) * mm, "end": v(23.34, -67.43) * mm});
            skLineSegment(sketch, "E582", {"start": v(30.21, -33.37) * mm, "end": v(34.02, -33.37) * mm});
            skLineSegment(sketch, "E583.MirrorCS", {"start": v(30.18, -59.49) * mm, "end": v(33.99, -59.49) * mm});
            skArc(sketch, "E584.MirrorCS", {"start": v(29.18, -60.49) * mm, "mid": v(29.47, -59.78) * mm, "end": v(30.18, -59.49) * mm});
            skArc(sketch, "E585.MirrorCS", {"start": v(33.99, -59.49) * mm, "mid": v(34.7, -59.78) * mm, "end": v(34.99, -60.49) * mm});
            skLineSegment(sketch, "E586.MirrorCS", {"start": v(30.18, -62.1) * mm, "end": v(33.99, -62.1) * mm});
            skArc(sketch, "E587.MirrorCS", {"start": v(29.18, -61.1) * mm, "mid": v(29.47, -61.8) * mm, "end": v(30.18, -62.1) * mm});
            skArc(sketch, "E588.MirrorCS", {"start": v(33.99, -62.1) * mm, "mid": v(34.7, -61.8) * mm, "end": v(34.99, -61.1) * mm});
            skLineSegment(sketch, "E589.MirrorCS", {"start": v(34.99, -61.1) * mm, "end": v(34.99, -60.49) * mm});
            skLineSegment(sketch, "E590.MirrorCS", {"start": v(29.18, -61.1) * mm, "end": v(29.18, -60.49) * mm});
            skLineSegment(sketch, "E591", {"start": v(30.84, -38.05) * mm, "end": v(31.27, -37.26) * mm});
            skLineSegment(sketch, "E592.trimOffspring", {"start": v(45.08, -53.29) * mm, "end": v(45.08, -23.43) * mm, "construction": true});
            skLineSegment(sketch, "E593.MirrorCS", {"start": v(30.84, -53.95) * mm, "end": v(31.27, -54.74) * mm});
            skLineSegment(sketch, "E594.MirrorCS", {"start": v(33.33, -38.05) * mm, "end": v(32.9, -37.26) * mm});
            skArc(sketch, "E595", {"start": v(32.9, -37.26) * mm, "mid": v(32.08, -36.78) * mm, "end": v(31.27, -37.26) * mm});
            skLineSegment(sketch, "E596.MirrorCS", {"start": v(33.33, -53.95) * mm, "end": v(32.9, -54.74) * mm});
            skArc(sketch, "E597.MirrorCS", {"start": v(32.9, -54.74) * mm, "mid": v(32.08, -55.22) * mm, "end": v(31.27, -54.74) * mm});
            skLineSegment(sketch, "E598.MirrorCS", {"start": v(40.04, -44.75) * mm, "end": v(40.83, -45.19) * mm});
            skLineSegment(sketch, "E599.MirrorCS", {"start": v(40.04, -47.25) * mm, "end": v(40.83, -46.81) * mm});
            skArc(sketch, "E600.MirrorCS", {"start": v(40.83, -45.19) * mm, "mid": v(41.3, -46) * mm, "end": v(40.83, -46.81) * mm});
            skLineSegment(sketch, "E601.MirrorCS", {"start": v(24.13, -44.75) * mm, "end": v(23.34, -45.19) * mm});
            skLineSegment(sketch, "E602.MirrorCS", {"start": v(24.13, -47.25) * mm, "end": v(23.34, -46.81) * mm});
            skArc(sketch, "E603.MirrorCS", {"start": v(23.34, -45.19) * mm, "mid": v(22.87, -46) * mm, "end": v(23.34, -46.81) * mm});
            skPoint(sketch, "E604.visualSharp", {"position": v(20.25, -38) * mm});
            skPoint(sketch, "E605.endSnap0", {"position": v(27.38, -50.7) * mm});
            skLineSegment(sketch, "E606", {"start": v(20.07, -39.15) * mm, "end": v(18.9, -49.61) * mm});
            skPoint(sketch, "E607.visualSharp", {"position": v(23.34, -56.74) * mm});
            skArc(sketch, "E607.filletArc", {"start": v(23.34, -57.5) * mm, "mid": v(23.2, -56.79) * mm, "end": v(22.83, -56.17) * mm});
            skArc(sketch, "E608.MirrorCS", {"start": v(40.83, -57.5) * mm, "mid": v(40.96, -56.79) * mm, "end": v(41.34, -56.17) * mm});
            skLineSegment(sketch, "E609.MirrorCS", {"start": v(40.83, -57.5) * mm, "end": v(40.83, -67.43) * mm});
            skLineSegment(sketch, "E610", {"start": v(23.34, -67.43) * mm, "end": v(40.83, -67.43) * mm});
            skPoint(sketch, "E611.visualSharp", {"position": v(27.16, -32.5) * mm});
            skPoint(sketch, "E612.visualSharp", {"position": v(29.02, -29.11) * mm});
            skLineSegment(sketch, "E613", {"start": v(25.69, -31.7) * mm, "end": v(21.39, -36.29) * mm});
            skLineSegment(sketch, "E614", {"start": v(22.83, -56.17) * mm, "end": v(20.36, -53.73) * mm});
            skPoint(sketch, "E615.visualSharp", {"position": v(18.63, -52.02) * mm});
            skArc(sketch, "E615.filletArc", {"start": v(18.9, -49.61) * mm, "mid": v(19.16, -51.84) * mm, "end": v(20.36, -53.73) * mm});
            skPoint(sketch, "E616.visualSharp", {"position": v(20.25, -37.5) * mm});
            skArc(sketch, "E616.filletArc", {"start": v(21.39, -36.29) * mm, "mid": v(20.5, -37.61) * mm, "end": v(20.07, -39.15) * mm});
            skLineSegment(sketch, "E617.MirrorCS", {"start": v(38.48, -31.7) * mm, "end": v(42.78, -36.29) * mm});
            skArc(sketch, "E618.MirrorCS", {"start": v(42.78, -36.29) * mm, "mid": v(43.68, -37.61) * mm, "end": v(44.1, -39.15) * mm});
            skLineSegment(sketch, "E619.MirrorCS", {"start": v(44.1, -39.15) * mm, "end": v(45.27, -49.61) * mm});
            skArc(sketch, "E620.MirrorCS", {"start": v(45.27, -49.61) * mm, "mid": v(45.01, -51.84) * mm, "end": v(43.81, -53.73) * mm});
            skLineSegment(sketch, "E621.MirrorCS", {"start": v(41.34, -56.17) * mm, "end": v(43.81, -53.73) * mm});
            skPoint(sketch, "E622.visualSharp", {"position": v(35.29, -29.35) * mm});
            skArc(sketch, "E623", {"start": v(25.69, -31.7) * mm, "mid": v(27.31, -30.34) * mm, "end": v(29.21, -29.4) * mm});
            skLineSegment(sketch, "E624", {"start": v(29.21, -31.75) * mm, "end": v(29.21, -29.4) * mm});
            skLineSegment(sketch, "E625", {"start": v(35.02, -31.75) * mm, "end": v(35.02, -29.43) * mm});
            skArc(sketch, "E626.trimOffspring", {"start": v(35.02, -29.43) * mm, "mid": v(36.89, -30.36) * mm, "end": v(38.48, -31.7) * mm});
            skPoint(sketch, "E627.visualSharp", {"position": v(49.74, -51.92) * mm});
            skSolve(sketch);
        }
        {
            var Q0;
            Q0=qCreatedBy(makeId("Top.planeOp"),FACE);
            var sketch = newSketch(context, id + "F5", { "sketchPlane" : qUnion([Q0])});
            skCircle(sketch, "E628", {"center": v(62.88, -46.43) * mm, "radius": 13.85 * mm, "construction": true});
            skLineSegment(sketch, "E629", {"start": v(62.88, -46.43) * mm, "end": v(74.2, -57.74) * mm, "construction": true});
            skArc(sketch, "E630", {"start": v(69.49, -51.13) * mm, "mid": v(67.58, -51.13) * mm, "end": v(67.58, -53.04) * mm});
            skArc(sketch, "E631", {"start": v(68.64, -54.1) * mm, "mid": v(70.55, -54.1) * mm, "end": v(70.55, -52.19) * mm});
            skLineSegment(sketch, "E632", {"start": v(67.58, -53.04) * mm, "end": v(68.64, -54.1) * mm});
            skLineSegment(sketch, "E633.MirrorCS", {"start": v(69.49, -51.13) * mm, "end": v(70.55, -52.19) * mm});
            skLineSegment(sketch, "E634.MirrorCS", {"start": v(56.27, -51.13) * mm, "end": v(55.2, -52.19) * mm});
            skArc(sketch, "E635.MirrorCS", {"start": v(57.12, -54.1) * mm, "mid": v(55.2, -54.1) * mm, "end": v(55.2, -52.19) * mm});
            skLineSegment(sketch, "E636.MirrorCS", {"start": v(58.18, -53.04) * mm, "end": v(57.12, -54.1) * mm});
            skArc(sketch, "E637.MirrorCS", {"start": v(56.27, -51.13) * mm, "mid": v(58.18, -51.13) * mm, "end": v(58.18, -53.04) * mm});
            skLineSegment(sketch, "E638.MirrorCS", {"start": v(58.18, -39.82) * mm, "end": v(57.12, -38.75) * mm});
            skLineSegment(sketch, "E639.MirrorCS", {"start": v(56.27, -41.72) * mm, "end": v(55.2, -40.66) * mm});
            skArc(sketch, "E640.MirrorCS", {"start": v(56.27, -41.72) * mm, "mid": v(58.18, -41.72) * mm, "end": v(58.18, -39.82) * mm});
            skArc(sketch, "E641.MirrorCS", {"start": v(57.12, -38.75) * mm, "mid": v(55.2, -38.75) * mm, "end": v(55.2, -40.66) * mm});
            skLineSegment(sketch, "E642.MirrorCS", {"start": v(67.58, -39.82) * mm, "end": v(68.64, -38.75) * mm});
            skLineSegment(sketch, "E643.MirrorCS", {"start": v(69.49, -41.72) * mm, "end": v(70.55, -40.66) * mm});
            skArc(sketch, "E644.MirrorCS", {"start": v(68.64, -38.75) * mm, "mid": v(70.55, -38.75) * mm, "end": v(70.55, -40.66) * mm});
            skArc(sketch, "E645.MirrorCS", {"start": v(69.49, -41.72) * mm, "mid": v(67.58, -41.72) * mm, "end": v(67.58, -39.82) * mm});
            skLineSegment(sketch, "E646", {"start": v(65.81, -32.18) * mm, "end": v(65.81, -32.8) * mm});
            skLineSegment(sketch, "E647", {"start": v(60, -32.18) * mm, "end": v(60, -32.8) * mm});
            skArc(sketch, "E648", {"start": v(64.38, -50.13) * mm, "mid": v(65.7, -49.26) * mm, "end": v(66.59, -47.93) * mm});
            skLineSegment(sketch, "E649.bottom", {"start": v(55.9, -44.93) * mm, "end": v(59.17, -44.93) * mm});
            skLineSegment(sketch, "E649.top", {"start": v(55.9, -47.93) * mm, "end": v(59.17, -47.93) * mm});
            skLineSegment(sketch, "E650.left", {"start": v(61.38, -39.44) * mm, "end": v(61.38, -42.72) * mm});
            skLineSegment(sketch, "E650.right", {"start": v(64.38, -39.44) * mm, "end": v(64.38, -42.72) * mm});
            skLineSegment(sketch, "E651.trimOffspring", {"start": v(66.59, -47.93) * mm, "end": v(69.86, -47.93) * mm});
            skLineSegment(sketch, "E652.trimOffspring", {"start": v(66.59, -44.93) * mm, "end": v(69.86, -44.93) * mm});
            skLineSegment(sketch, "E653.trimOffspring", {"start": v(64.38, -50.13) * mm, "end": v(64.38, -53.4) * mm});
            skLineSegment(sketch, "E654.trimOffspring", {"start": v(61.38, -50.13) * mm, "end": v(61.38, -53.4) * mm});
            skArc(sketch, "E655.trimOffspring", {"start": v(66.59, -44.93) * mm, "mid": v(65.7, -43.6) * mm, "end": v(64.38, -42.72) * mm});
            skArc(sketch, "E656.trimOffspring", {"start": v(61.38, -42.72) * mm, "mid": v(60.05, -43.6) * mm, "end": v(59.17, -44.93) * mm});
            skArc(sketch, "E657.trimOffspring", {"start": v(59.17, -47.93) * mm, "mid": v(60.05, -49.26) * mm, "end": v(61.38, -50.13) * mm});
            skArc(sketch, "E658", {"start": v(72.15, -46.94) * mm, "mid": v(72.2, -46.9) * mm, "end": v(72.26, -46.87) * mm});
            skArc(sketch, "E659.filletArc", {"start": v(69.86, -47.93) * mm, "mid": v(70.36, -47.86) * mm, "end": v(70.83, -47.68) * mm});
            skArc(sketch, "E660.filletArc", {"start": v(70.83, -45.18) * mm, "mid": v(70.36, -45) * mm, "end": v(69.86, -44.93) * mm});
            skArc(sketch, "E661.MirrorCS", {"start": v(54.93, -45.18) * mm, "mid": v(55.4, -45) * mm, "end": v(55.9, -44.93) * mm});
            skArc(sketch, "E662.MirrorCS", {"start": v(55.9, -47.93) * mm, "mid": v(55.4, -47.86) * mm, "end": v(54.93, -47.68) * mm});
            skArc(sketch, "E663.MirrorCS", {"start": v(53.6, -46.94) * mm, "mid": v(53.55, -46.9) * mm, "end": v(53.5, -46.87) * mm});
            skArc(sketch, "E664.MirrorCS", {"start": v(64.13, -54.38) * mm, "mid": v(64.31, -53.91) * mm, "end": v(64.38, -53.4) * mm});
            skArc(sketch, "E665.MirrorCS", {"start": v(61.38, -53.4) * mm, "mid": v(61.44, -53.91) * mm, "end": v(61.63, -54.38) * mm});
            skArc(sketch, "E666.MirrorCS", {"start": v(61.38, -39.44) * mm, "mid": v(61.44, -38.94) * mm, "end": v(61.63, -38.47) * mm});
            skArc(sketch, "E667.MirrorCS", {"start": v(64.13, -38.47) * mm, "mid": v(64.31, -38.94) * mm, "end": v(64.38, -39.44) * mm});
            skArc(sketch, "E668.filletArc", {"start": v(64.81, -33.8) * mm, "mid": v(65.52, -33.5) * mm, "end": v(65.81, -32.8) * mm});
            skArc(sketch, "E669.filletArc", {"start": v(60, -32.8) * mm, "mid": v(60.3, -33.5) * mm, "end": v(61, -33.8) * mm});
            skCircle(sketch, "E670", {"center": v(62.88, -46.43) * mm, "radius": 8 * mm, "construction": true});
            skLineSegment(sketch, "E671.MirrorCS", {"start": v(54.13, -57.93) * mm, "end": v(54.13, -67.86) * mm});
            skLineSegment(sketch, "E672", {"start": v(61, -33.8) * mm, "end": v(64.81, -33.8) * mm});
            skLineSegment(sketch, "E673.MirrorCS", {"start": v(60.97, -59.92) * mm, "end": v(64.78, -59.92) * mm});
            skArc(sketch, "E674.MirrorCS", {"start": v(59.97, -60.92) * mm, "mid": v(60.27, -60.2) * mm, "end": v(60.97, -59.92) * mm});
            skArc(sketch, "E675.MirrorCS", {"start": v(64.78, -59.92) * mm, "mid": v(65.5, -60.2) * mm, "end": v(65.78, -60.92) * mm});
            skLineSegment(sketch, "E676.MirrorCS", {"start": v(60.97, -62.53) * mm, "end": v(64.78, -62.53) * mm});
            skArc(sketch, "E677.MirrorCS", {"start": v(59.97, -61.53) * mm, "mid": v(60.27, -62.24) * mm, "end": v(60.97, -62.53) * mm});
            skArc(sketch, "E678.MirrorCS", {"start": v(64.78, -62.53) * mm, "mid": v(65.5, -62.24) * mm, "end": v(65.78, -61.53) * mm});
            skLineSegment(sketch, "E679.MirrorCS", {"start": v(65.78, -61.53) * mm, "end": v(65.78, -60.92) * mm});
            skLineSegment(sketch, "E680.MirrorCS", {"start": v(59.97, -61.53) * mm, "end": v(59.97, -60.92) * mm});
            skLineSegment(sketch, "E681", {"start": v(61.63, -38.47) * mm, "end": v(62.07, -37.69) * mm});
            skLineSegment(sketch, "E682.trimOffspring", {"start": v(75.88, -53.72) * mm, "end": v(75.88, -23.85) * mm, "construction": true});
            skLineSegment(sketch, "E683.MirrorCS", {"start": v(61.63, -54.38) * mm, "end": v(62.07, -55.17) * mm});
            skLineSegment(sketch, "E684.MirrorCS", {"start": v(64.13, -38.47) * mm, "end": v(63.7, -37.69) * mm});
            skArc(sketch, "E685", {"start": v(63.7, -37.69) * mm, "mid": v(62.88, -37.2) * mm, "end": v(62.07, -37.69) * mm});
            skLineSegment(sketch, "E686.MirrorCS", {"start": v(64.13, -54.38) * mm, "end": v(63.7, -55.17) * mm});
            skArc(sketch, "E687.MirrorCS", {"start": v(63.7, -55.17) * mm, "mid": v(62.88, -55.65) * mm, "end": v(62.07, -55.17) * mm});
            skLineSegment(sketch, "E688.MirrorCS", {"start": v(70.83, -45.18) * mm, "end": v(71.62, -45.61) * mm});
            skLineSegment(sketch, "E689.MirrorCS", {"start": v(70.83, -47.68) * mm, "end": v(71.62, -47.24) * mm});
            skArc(sketch, "E690.MirrorCS", {"start": v(71.62, -45.61) * mm, "mid": v(72.1, -46.43) * mm, "end": v(71.62, -47.24) * mm});
            skLineSegment(sketch, "E691.MirrorCS", {"start": v(54.93, -45.18) * mm, "end": v(54.14, -45.61) * mm});
            skLineSegment(sketch, "E692.MirrorCS", {"start": v(54.93, -47.68) * mm, "end": v(54.14, -47.24) * mm});
            skArc(sketch, "E693.MirrorCS", {"start": v(54.14, -45.61) * mm, "mid": v(53.66, -46.43) * mm, "end": v(54.14, -47.24) * mm});
            skPoint(sketch, "E694.visualSharp", {"position": v(51.04, -38.42) * mm});
            skPoint(sketch, "E695.endSnap0", {"position": v(58.18, -51.13) * mm});
            skLineSegment(sketch, "E696", {"start": v(50.86, -39.58) * mm, "end": v(49.7, -50.04) * mm});
            skPoint(sketch, "E697.visualSharp", {"position": v(54.13, -57.17) * mm});
            skArc(sketch, "E697.filletArc", {"start": v(54.13, -57.93) * mm, "mid": v(54, -57.22) * mm, "end": v(53.63, -56.6) * mm});
            skArc(sketch, "E698.MirrorCS", {"start": v(71.62, -57.93) * mm, "mid": v(71.75, -57.22) * mm, "end": v(72.13, -56.6) * mm});
            skLineSegment(sketch, "E699.MirrorCS", {"start": v(71.62, -57.93) * mm, "end": v(71.62, -67.86) * mm});
            skLineSegment(sketch, "E700", {"start": v(54.13, -67.86) * mm, "end": v(71.62, -67.86) * mm});
            skPoint(sketch, "E701.visualSharp", {"position": v(57.96, -32.93) * mm});
            skPoint(sketch, "E702.visualSharp", {"position": v(59.8, -29.54) * mm});
            skLineSegment(sketch, "E703", {"start": v(53.63, -56.6) * mm, "end": v(51.15, -54.16) * mm});
            skPoint(sketch, "E704.visualSharp", {"position": v(49.42, -52.45) * mm});
            skArc(sketch, "E704.filletArc", {"start": v(49.7, -50.04) * mm, "mid": v(49.95, -52.27) * mm, "end": v(51.15, -54.16) * mm});
            skPoint(sketch, "E705.visualSharp", {"position": v(51.04, -37.93) * mm});
            skArc(sketch, "E705.filletArc", {"start": v(52.18, -36.71) * mm, "mid": v(51.29, -38.04) * mm, "end": v(50.86, -39.58) * mm});
            skArc(sketch, "E706.MirrorCS", {"start": v(73.58, -36.71) * mm, "mid": v(74.47, -38.04) * mm, "end": v(74.9, -39.58) * mm});
            skLineSegment(sketch, "E707.MirrorCS", {"start": v(74.9, -39.58) * mm, "end": v(76.06, -50.04) * mm});
            skArc(sketch, "E708.MirrorCS", {"start": v(76.06, -50.04) * mm, "mid": v(75.8, -52.27) * mm, "end": v(74.6, -54.16) * mm});
            skLineSegment(sketch, "E709.MirrorCS", {"start": v(72.13, -56.6) * mm, "end": v(74.6, -54.16) * mm});
            skPoint(sketch, "E710.visualSharp", {"position": v(66.08, -29.78) * mm});
            skArc(sketch, "E711", {"start": v(56.9, -31.7) * mm, "mid": v(58.36, -30.6) * mm, "end": v(60, -29.84) * mm});
            skLineSegment(sketch, "E712", {"start": v(60, -32.18) * mm, "end": v(60, -29.84) * mm});
            skLineSegment(sketch, "E713", {"start": v(65.81, -32.18) * mm, "end": v(65.81, -29.86) * mm});
            skArc(sketch, "E714.trimOffspring", {"start": v(65.81, -29.86) * mm, "mid": v(67.43, -30.62) * mm, "end": v(68.85, -31.7) * mm});
            skPoint(sketch, "E715.visualSharp", {"position": v(80.53, -52.35) * mm});
            skFitSpline(sketch, "E716", {"points": [v(52.18, -36.71) * mm, v(56.48, -32.12) * mm], "startDerivative": vector(4.3, 4.6) * mm, "endDerivative": vector(1.45, 6.85) * mm});
            skLineSegment(sketch, "E717", {"start": v(62.88, -46.43) * mm, "end": v(62.88, -23.32) * mm, "construction": true});
            skFitSpline(sketch, "E718.MirrorCS", {"points": [v(73.58, -36.71) * mm, v(69.27, -32.12) * mm], "startDerivative": vector(-4.3, 4.6) * mm, "endDerivative": vector(-1.45, 6.85) * mm});
            skArc(sketch, "E719.filletArc", {"start": v(56.9, -31.7) * mm, "mid": v(56.59, -32.08) * mm, "end": v(56.37, -32.53) * mm});
            skArc(sketch, "E720.filletArc", {"start": v(69.38, -32.53) * mm, "mid": v(69.17, -32.08) * mm, "end": v(68.85, -31.7) * mm});
            skSolve(sketch);
        }
        {
            var Q0;
            Q0 = qSketchRegion(id + "F5", true);
            extrude(context, id + "F6", {"entities" : qUnion([Q0]), "depth" : 3 * mm, "offsetDistance" : 25 * mm});
        }
        {
            var Q0;
            Q0 = qSketchRegion(id + "F4", true);
            extrude(context, id + "F7", {"entities" : qUnion([Q0]), "depth" : 3 * mm, "offsetDistance" : 25 * mm});
        }
        {
            var Q0;
            Q0 = qSketchRegion(id + "F3", true);
            extrude(context, id + "F8", {"entities" : qUnion([Q0]), "depth" : 3 * mm, "offsetDistance" : 25 * mm});
        }
        {
            var Q0;
            Q0 = qSketchRegion(id + "F2", true);
            extrude(context, id + "F9", {"entities" : qUnion([Q0]), "depth" : 3 * mm, "offsetDistance" : 25 * mm});
        }
        {
            var Q0;
            Q0 = qSketchRegion(id + "F1", true);
            extrude(context, id + "F10", {"entities" : qUnion([Q0]), "depth" : 3 * mm, "offsetDistance" : 25 * mm});
        }
        {
            var Q0;
            Q0 = qSketchRegion(id + "F0", true);
            extrude(context, id + "F11", {"entities" : qUnion([Q0]), "depth" : 3 * mm, "offsetDistance" : 25 * mm});
        }
        {
            var Q0;
            Q0=makeQuery(id+"F10.opExtrude","CAP_FACE",FACE,{"disambiguationData":[OSD([sQuery(id+"F1.wireOp",EDGE,"E86"),sQuery(id+"F1.wireOp",EDGE,"E87"),sQuery(id+"F1.wireOp",EDGE,"E89"),sQuery(id+"F1.wireOp",EDGE,"E90.MirrorCS"),sQuery(id+"F1.wireOp",EDGE,"E91.MirrorCS"),sQuery(id+"F1.wireOp",EDGE,"E92.MirrorCS"),sQuery(id+"F1.wireOp",EDGE,"E93.MirrorCS"),sQuery(id+"F1.wireOp",EDGE,"E94.MirrorCS"),sQuery(id+"F1.wireOp",EDGE,"E95.MirrorCS"),sQuery(id+"F1.wireOp",EDGE,"E96.MirrorCS"),sQuery(id+"F1.wireOp",EDGE,"E97.MirrorCS"),sQuery(id+"F1.wireOp",EDGE,"E98.MirrorCS"),sQuery(id+"F1.wireOp",EDGE,"E99.MirrorCS"),sQuery(id+"F1.wireOp",EDGE,"E100.MirrorCS"),sQuery(id+"F1.wireOp",EDGE,"E101.MirrorCS"),sQuery(id+"F1.wireOp",EDGE,"E102.MirrorCS"),sQuery(id+"F1.wireOp",EDGE,"E103"),sQuery(id+"F1.wireOp",EDGE,"E104"),sQuery(id+"F1.wireOp",EDGE,"E105"),sQuery(id+"F1.wireOp",EDGE,"E106"),sQuery(id+"F1.wireOp",EDGE,"E107.bottom"),sQuery(id+"F1.wireOp",EDGE,"E107.top"),sQuery(id+"F1.wireOp",EDGE,"E108.left"),sQuery(id+"F1.wireOp",EDGE,"E108.right"),sQuery(id+"F1.wireOp",EDGE,"E109.trimOffspring"),sQuery(id+"F1.wireOp",EDGE,"E110.trimOffspring"),sQuery(id+"F1.wireOp",EDGE,"E111.trimOffspring"),sQuery(id+"F1.wireOp",EDGE,"E112.trimOffspring"),sQuery(id+"F1.wireOp",EDGE,"E113.trimOffspring"),sQuery(id+"F1.wireOp",EDGE,"E114.trimOffspring"),sQuery(id+"F1.wireOp",EDGE,"E115.trimOffspring"),sQuery(id+"F1.wireOp",EDGE,"E117.filletArc"),sQuery(id+"F1.wireOp",EDGE,"E118.filletArc"),sQuery(id+"F1.wireOp",EDGE,"E119.MirrorCS"),sQuery(id+"F1.wireOp",EDGE,"E120.MirrorCS"),sQuery(id+"F1.wireOp",EDGE,"E122.MirrorCS"),sQuery(id+"F1.wireOp",EDGE,"E123.MirrorCS"),sQuery(id+"F1.wireOp",EDGE,"E124.MirrorCS"),sQuery(id+"F1.wireOp",EDGE,"E125.MirrorCS"),sQuery(id+"F1.wireOp",EDGE,"E126.filletArc"),sQuery(id+"F1.wireOp",EDGE,"E127.filletArc"),sQuery(id+"F1.wireOp",EDGE,"E129"),sQuery(id+"F1.wireOp",EDGE,"E130.filletArc"),sQuery(id+"F1.wireOp",EDGE,"E131.MirrorCS"),sQuery(id+"F1.wireOp",EDGE,"E132"),sQuery(id+"F1.wireOp",EDGE,"E133.filletArc"),sQuery(id+"F1.wireOp",EDGE,"E134"),sQuery(id+"F1.wireOp",EDGE,"E135"),sQuery(id+"F1.wireOp",EDGE,"E136.filletArc"),sQuery(id+"F1.wireOp",EDGE,"E137.MirrorCS"),sQuery(id+"F1.wireOp",EDGE,"E138.MirrorCS"),sQuery(id+"F1.wireOp",EDGE,"E139.MirrorCS"),sQuery(id+"F1.wireOp",EDGE,"E140.MirrorCS"),sQuery(id+"F1.wireOp",EDGE,"E141.MirrorCS"),sQuery(id+"F1.wireOp",EDGE,"E143"),sQuery(id+"F1.wireOp",EDGE,"E145.MirrorCS"),sQuery(id+"F1.wireOp",EDGE,"E146.MirrorCS"),sQuery(id+"F1.wireOp",EDGE,"E147.MirrorCS"),sQuery(id+"F1.wireOp",EDGE,"E148.MirrorCS"),sQuery(id+"F1.wireOp",EDGE,"E149.MirrorCS"),sQuery(id+"F1.wireOp",EDGE,"E150.MirrorCS"),sQuery(id+"F1.wireOp",EDGE,"E151.MirrorCS"),sQuery(id+"F1.wireOp",EDGE,"E152.MirrorCS"),sQuery(id+"F1.wireOp",EDGE,"E153.MirrorCS"),sQuery(id+"F1.wireOp",EDGE,"E154.MirrorCS"),sQuery(id+"F1.wireOp",EDGE,"E155.MirrorCS"),sQuery(id+"F1.wireOp",EDGE,"E156"),sQuery(id+"F1.wireOp",EDGE,"E158.MirrorCS"),sQuery(id+"F1.wireOp",EDGE,"E159.MirrorCS"),sQuery(id+"F1.wireOp",EDGE,"E160"),sQuery(id+"F1.wireOp",EDGE,"E161.MirrorCS"),sQuery(id+"F1.wireOp",EDGE,"E162.MirrorCS"),sQuery(id+"F1.wireOp",EDGE,"E163.MirrorCS"),sQuery(id+"F1.wireOp",EDGE,"E164.MirrorCS"),sQuery(id+"F1.wireOp",EDGE,"E165.MirrorCS"),sQuery(id+"F1.wireOp",EDGE,"E166.MirrorCS"),sQuery(id+"F1.wireOp",EDGE,"E167.MirrorCS"),sQuery(id+"F1.wireOp",EDGE,"E168.MirrorCS"),sQuery(id+"F1.wireOp",EDGE,"E169")])],"isStart":false});
            var sketch = newSketch(context, id + "F12", { "sketchPlane" : qUnion([Q0])});
            skArc(sketch, "E721", {"start": v(29.83, 3.58) * mm, "mid": v(28.78, 2.83) * mm, "end": v(28.03, 1.78) * mm});
            skLineSegment(sketch, "E722", {"start": v(31.61, 0) * mm, "end": v(-1.84, 33.45) * mm, "construction": true});
            skArc(sketch, "E723.trimOffspring", {"start": v(35.22, 1.72) * mm, "mid": v(34.44, 2.83) * mm, "end": v(33.33, 3.61) * mm});
            skArc(sketch, "E724.trimOffspring", {"start": v(33.4, -3.58) * mm, "mid": v(34.44, -2.83) * mm, "end": v(35.2, -1.78) * mm});
            skArc(sketch, "E725.trimOffspring", {"start": v(28, -1.72) * mm, "mid": v(28.78, -2.83) * mm, "end": v(29.9, -3.61) * mm});
            skArc(sketch, "E726", {"start": v(39.39, 5.66) * mm, "mid": v(39.39, 7.78) * mm, "end": v(37.27, 7.78) * mm});
            skPoint(sketch, "E727.center.orphan", {"position": v(37.27, 5.66) * mm});
            skArc(sketch, "E728", {"start": v(36.2, 6.72) * mm, "mid": v(36.2, 4.6) * mm, "end": v(38.33, 4.6) * mm});
            skLineSegment(sketch, "E729", {"start": v(39.39, 5.66) * mm, "end": v(38.33, 4.6) * mm});
            skLineSegment(sketch, "E730", {"start": v(37.27, 7.78) * mm, "end": v(36.2, 6.72) * mm});
            skArc(sketch, "E731", {"start": v(42.56, 4.39) * mm, "mid": v(40.2, 8.09) * mm, "end": v(36.65, 10.67) * mm});
            skLineSegment(sketch, "E732", {"start": v(33.33, 3.61) * mm, "end": v(33.33, 7.61) * mm});
            skLineSegment(sketch, "E733", {"start": v(29.83, 3.58) * mm, "end": v(29.83, 7.58) * mm});
            skArc(sketch, "E734", {"start": v(33.33, 7.61) * mm, "mid": v(31.56, 9.36) * mm, "end": v(29.83, 7.58) * mm});
            skArc(sketch, "E735", {"start": v(34.18, 9.83) * mm, "mid": v(32.9, 10.08) * mm, "end": v(31.61, 10.16) * mm});
            skLineSegment(sketch, "E736", {"start": v(35.52, 10.47) * mm, "end": v(35.14, 10.1) * mm});
            skPoint(sketch, "E737.visualSharp", {"position": v(34.72, 9.68) * mm});
            skArc(sketch, "E737.filletArc", {"start": v(34.18, 9.83) * mm, "mid": v(34.7, 9.84) * mm, "end": v(35.14, 10.1) * mm});
            skPoint(sketch, "E738.visualSharp", {"position": v(36, 10.95) * mm});
            skArc(sketch, "E738.filletArc", {"start": v(36.65, 10.67) * mm, "mid": v(36.05, 10.75) * mm, "end": v(35.52, 10.47) * mm});
            skLineSegment(sketch, "E739.MirrorCS", {"start": v(42.08, 3.9) * mm, "end": v(41.7, 3.53) * mm});
            skArc(sketch, "E740.MirrorCS", {"start": v(41.44, 2.57) * mm, "mid": v(41.45, 3.08) * mm, "end": v(41.7, 3.53) * mm});
            skArc(sketch, "E741.MirrorCS", {"start": v(41.44, 2.57) * mm, "mid": v(41.7, 1.3) * mm, "end": v(41.77, 0) * mm});
            skPoint(sketch, "E742.MirrorP", {"position": v(41.29, 3.11) * mm});
            skPoint(sketch, "E743.MirrorP", {"position": v(42.56, 4.39) * mm});
            skArc(sketch, "E744.MirrorCS", {"start": v(42.28, 5.04) * mm, "mid": v(42.36, 4.44) * mm, "end": v(42.08, 3.9) * mm});
            skLineSegment(sketch, "E745.MirrorCS", {"start": v(35.22, 1.72) * mm, "end": v(39.22, 1.72) * mm});
            skArc(sketch, "E746.MirrorCS", {"start": v(39.22, 1.72) * mm, "mid": v(40.97, -0.05) * mm, "end": v(39.2, -1.78) * mm});
            skLineSegment(sketch, "E747.MirrorCS", {"start": v(35.2, -1.78) * mm, "end": v(39.2, -1.78) * mm});
            skLineSegment(sketch, "E748.MirrorCS", {"start": v(27.7, -10.47) * mm, "end": v(28.08, -10.1) * mm});
            skLineSegment(sketch, "E749.MirrorCS", {"start": v(21.14, -3.9) * mm, "end": v(21.52, -3.53) * mm});
            skArc(sketch, "E750.MirrorCS", {"start": v(21.78, -2.57) * mm, "mid": v(21.77, -3.08) * mm, "end": v(21.52, -3.53) * mm});
            skPoint(sketch, "E751.MirrorP", {"position": v(27.22, -10.95) * mm});
            skArc(sketch, "E752.MirrorCS", {"start": v(20.94, -5.04) * mm, "mid": v(20.86, -4.44) * mm, "end": v(21.14, -3.9) * mm});
            skArc(sketch, "E753.MirrorCS", {"start": v(26.57, -10.67) * mm, "mid": v(27.17, -10.75) * mm, "end": v(27.7, -10.47) * mm});
            skArc(sketch, "E754.MirrorCS", {"start": v(29.04, -9.83) * mm, "mid": v(28.53, -9.84) * mm, "end": v(28.08, -10.1) * mm});
            skArc(sketch, "E755.MirrorCS", {"start": v(24, -1.72) * mm, "mid": v(22.25, 0.05) * mm, "end": v(24.03, 1.78) * mm});
            skArc(sketch, "E756.MirrorCS", {"start": v(21.78, -2.57) * mm, "mid": v(21.53, -1.3) * mm, "end": v(21.45, 0) * mm});
            skPoint(sketch, "E757.MirrorP", {"position": v(21.93, -3.11) * mm});
            skLineSegment(sketch, "E758.MirrorCS", {"start": v(25.95, -7.78) * mm, "end": v(27.01, -6.72) * mm});
            skArc(sketch, "E759.MirrorCS", {"start": v(29.9, -3.61) * mm, "mid": v(28.78, -2.83) * mm, "end": v(28, -1.72) * mm});
            skLineSegment(sketch, "E760.MirrorCS", {"start": v(23.83, -5.66) * mm, "end": v(24.9, -4.6) * mm});
            skArc(sketch, "E761.MirrorCS", {"start": v(24.9, -4.6) * mm, "mid": v(27.01, -4.6) * mm, "end": v(27.01, -6.72) * mm});
            skPoint(sketch, "E762.MirrorP", {"position": v(20.66, -4.39) * mm});
            skArc(sketch, "E763.MirrorCS", {"start": v(29.04, -9.83) * mm, "mid": v(30.32, -10.08) * mm, "end": v(31.61, -10.16) * mm});
            skLineSegment(sketch, "E764.MirrorCS", {"start": v(28, -1.72) * mm, "end": v(24, -1.72) * mm});
            skPoint(sketch, "E765.MirrorP", {"position": v(28.5, -9.68) * mm});
            skArc(sketch, "E766.MirrorCS", {"start": v(25.95, -7.78) * mm, "mid": v(23.83, -7.78) * mm, "end": v(23.83, -5.66) * mm});
            skArc(sketch, "E767.MirrorCS", {"start": v(29.9, -7.61) * mm, "mid": v(31.66, -9.36) * mm, "end": v(33.4, -7.58) * mm});
            skLineSegment(sketch, "E768.MirrorCS", {"start": v(29.9, -3.61) * mm, "end": v(29.9, -7.61) * mm});
            skLineSegment(sketch, "E769.MirrorCS", {"start": v(28.03, 1.78) * mm, "end": v(24.03, 1.78) * mm});
            skLineSegment(sketch, "E770.MirrorCS", {"start": v(33.4, -3.58) * mm, "end": v(33.4, -7.58) * mm});
            skArc(sketch, "E771.MirrorCS", {"start": v(27.22, -10.95) * mm, "mid": v(23.52, -8.6) * mm, "end": v(20.94, -5.04) * mm});
            skLineSegment(sketch, "E772.MirrorCS", {"start": v(42.08, -3.9) * mm, "end": v(41.7, -3.53) * mm});
            skLineSegment(sketch, "E773.MirrorCS", {"start": v(35.52, -10.47) * mm, "end": v(35.14, -10.1) * mm});
            skArc(sketch, "E774.MirrorCS", {"start": v(41.44, -2.57) * mm, "mid": v(41.45, -3.08) * mm, "end": v(41.7, -3.53) * mm});
            skArc(sketch, "E775.MirrorCS", {"start": v(36.65, -10.67) * mm, "mid": v(36.05, -10.75) * mm, "end": v(35.52, -10.47) * mm});
            skArc(sketch, "E776.MirrorCS", {"start": v(42.28, -5.04) * mm, "mid": v(42.36, -4.44) * mm, "end": v(42.08, -3.9) * mm});
            skPoint(sketch, "E777.MirrorP", {"position": v(42.56, -4.39) * mm});
            skArc(sketch, "E778.MirrorCS", {"start": v(34.18, -9.83) * mm, "mid": v(34.7, -9.84) * mm, "end": v(35.14, -10.1) * mm});
            skArc(sketch, "E779.MirrorCS", {"start": v(34.18, -9.83) * mm, "mid": v(32.9, -10.08) * mm, "end": v(31.61, -10.16) * mm});
            skLineSegment(sketch, "E780.MirrorCS", {"start": v(39.39, -5.66) * mm, "end": v(38.33, -4.6) * mm});
            skPoint(sketch, "E781.MirrorP", {"position": v(34.72, -9.68) * mm});
            skArc(sketch, "E782.MirrorCS", {"start": v(42.28, -5.04) * mm, "mid": v(39.95, -8.34) * mm, "end": v(36.65, -10.67) * mm});
            skPoint(sketch, "E783.MirrorP", {"position": v(36, -10.95) * mm});
            skPoint(sketch, "E784.MirrorP", {"position": v(37.27, -5.66) * mm});
            skArc(sketch, "E785.MirrorCS", {"start": v(41.44, -2.57) * mm, "mid": v(41.7, -1.3) * mm, "end": v(41.77, 0) * mm});
            skPoint(sketch, "E786.MirrorP", {"position": v(41.29, -3.11) * mm});
            skLineSegment(sketch, "E787.MirrorCS", {"start": v(37.27, -7.78) * mm, "end": v(36.2, -6.72) * mm});
            skArc(sketch, "E788.MirrorCS", {"start": v(39.39, -5.66) * mm, "mid": v(39.39, -7.78) * mm, "end": v(37.27, -7.78) * mm});
            skArc(sketch, "E789.MirrorCS", {"start": v(36.2, -6.72) * mm, "mid": v(36.2, -4.6) * mm, "end": v(38.33, -4.6) * mm});
            skLineSegment(sketch, "E790.MirrorCS", {"start": v(25.95, 7.78) * mm, "end": v(27.01, 6.72) * mm});
            skLineSegment(sketch, "E791.MirrorCS", {"start": v(23.83, 5.66) * mm, "end": v(24.9, 4.6) * mm});
            skArc(sketch, "E792.MirrorCS", {"start": v(24.9, 4.6) * mm, "mid": v(27.01, 4.6) * mm, "end": v(27.01, 6.72) * mm});
            skArc(sketch, "E793.MirrorCS", {"start": v(25.95, 7.78) * mm, "mid": v(23.83, 7.78) * mm, "end": v(23.83, 5.66) * mm});
            skArc(sketch, "E794.MirrorCS", {"start": v(29.04, 9.83) * mm, "mid": v(30.32, 10.08) * mm, "end": v(31.61, 10.16) * mm});
            skLineSegment(sketch, "E795.MirrorCS", {"start": v(31.61, 0) * mm, "end": v(65.06, -33.45) * mm, "construction": true});
            skLineSegment(sketch, "E796.MirrorCS", {"start": v(21.14, 3.9) * mm, "end": v(21.52, 3.53) * mm});
            skArc(sketch, "E797.MirrorCS", {"start": v(21.78, 2.57) * mm, "mid": v(21.77, 3.08) * mm, "end": v(21.52, 3.53) * mm});
            skPoint(sketch, "E798.MirrorP", {"position": v(21.93, 3.11) * mm});
            skPoint(sketch, "E799.MirrorP", {"position": v(20.66, 4.39) * mm});
            skArc(sketch, "E800.MirrorCS", {"start": v(21.78, 2.57) * mm, "mid": v(21.53, 1.3) * mm, "end": v(21.45, 0) * mm});
            skLineSegment(sketch, "E801.MirrorCS", {"start": v(27.7, 10.47) * mm, "end": v(28.08, 10.1) * mm});
            skArc(sketch, "E802.MirrorCS", {"start": v(26.57, 10.67) * mm, "mid": v(27.17, 10.75) * mm, "end": v(27.7, 10.47) * mm});
            skArc(sketch, "E803.MirrorCS", {"start": v(29.04, 9.83) * mm, "mid": v(28.53, 9.84) * mm, "end": v(28.08, 10.1) * mm});
            skPoint(sketch, "E804.MirrorP", {"position": v(27.22, 10.95) * mm});
            skPoint(sketch, "E805.MirrorP", {"position": v(28.5, 9.68) * mm});
            skArc(sketch, "E806.MirrorCS", {"start": v(26.57, 10.67) * mm, "mid": v(23.27, 8.34) * mm, "end": v(20.94, 5.04) * mm});
            skArc(sketch, "E807.MirrorCS", {"start": v(20.94, 5.04) * mm, "mid": v(20.86, 4.44) * mm, "end": v(21.14, 3.9) * mm});
            skLineSegment(sketch, "E808.0", {"start": v(36.2, 6.72) * mm, "end": v(38.33, 4.6) * mm, "construction": true});
            skLineSegment(sketch, "E809.0", {"start": v(37.27, 7.78) * mm, "end": v(39.39, 5.66) * mm, "construction": true});
            skSolve(sketch);
        }
        {
            var Q0;
            Q0=makeQuery(id+"F8.opExtrude","CAP_FACE",FACE,{"disambiguationData":[OSD([sQuery(id+"F3.wireOp",EDGE,"E355"),sQuery(id+"F3.wireOp",EDGE,"E356"),sQuery(id+"F3.wireOp",EDGE,"E357"),sQuery(id+"F3.wireOp",EDGE,"E358.MirrorCS"),sQuery(id+"F3.wireOp",EDGE,"E359.MirrorCS"),sQuery(id+"F3.wireOp",EDGE,"E360.MirrorCS"),sQuery(id+"F3.wireOp",EDGE,"E361.MirrorCS"),sQuery(id+"F3.wireOp",EDGE,"E362.MirrorCS"),sQuery(id+"F3.wireOp",EDGE,"E363.MirrorCS"),sQuery(id+"F3.wireOp",EDGE,"E364.MirrorCS"),sQuery(id+"F3.wireOp",EDGE,"E365.MirrorCS"),sQuery(id+"F3.wireOp",EDGE,"E366.MirrorCS"),sQuery(id+"F3.wireOp",EDGE,"E367.MirrorCS"),sQuery(id+"F3.wireOp",EDGE,"E368.MirrorCS"),sQuery(id+"F3.wireOp",EDGE,"E369.MirrorCS"),sQuery(id+"F3.wireOp",EDGE,"E370.MirrorCS"),sQuery(id+"F3.wireOp",EDGE,"E371"),sQuery(id+"F3.wireOp",EDGE,"E372"),sQuery(id+"F3.wireOp",EDGE,"E373"),sQuery(id+"F3.wireOp",EDGE,"E374.bottom"),sQuery(id+"F3.wireOp",EDGE,"E374.top"),sQuery(id+"F3.wireOp",EDGE,"E375.left"),sQuery(id+"F3.wireOp",EDGE,"E375.right"),sQuery(id+"F3.wireOp",EDGE,"E376.trimOffspring"),sQuery(id+"F3.wireOp",EDGE,"E377.trimOffspring"),sQuery(id+"F3.wireOp",EDGE,"E378.trimOffspring"),sQuery(id+"F3.wireOp",EDGE,"E379.trimOffspring"),sQuery(id+"F3.wireOp",EDGE,"E380.trimOffspring"),sQuery(id+"F3.wireOp",EDGE,"E381.trimOffspring"),sQuery(id+"F3.wireOp",EDGE,"E382.trimOffspring"),sQuery(id+"F3.wireOp",EDGE,"E384.filletArc"),sQuery(id+"F3.wireOp",EDGE,"E385.filletArc"),sQuery(id+"F3.wireOp",EDGE,"E386.MirrorCS"),sQuery(id+"F3.wireOp",EDGE,"E387.MirrorCS"),sQuery(id+"F3.wireOp",EDGE,"E389.MirrorCS"),sQuery(id+"F3.wireOp",EDGE,"E390.MirrorCS"),sQuery(id+"F3.wireOp",EDGE,"E391.MirrorCS"),sQuery(id+"F3.wireOp",EDGE,"E392.MirrorCS"),sQuery(id+"F3.wireOp",EDGE,"E393.filletArc"),sQuery(id+"F3.wireOp",EDGE,"E394.filletArc"),sQuery(id+"F3.wireOp",EDGE,"E396.MirrorCS"),sQuery(id+"F3.wireOp",EDGE,"E397"),sQuery(id+"F3.wireOp",EDGE,"E398.MirrorCS"),sQuery(id+"F3.wireOp",EDGE,"E399.MirrorCS"),sQuery(id+"F3.wireOp",EDGE,"E400.MirrorCS"),sQuery(id+"F3.wireOp",EDGE,"E401.MirrorCS"),sQuery(id+"F3.wireOp",EDGE,"E402.MirrorCS"),sQuery(id+"F3.wireOp",EDGE,"E403.MirrorCS"),sQuery(id+"F3.wireOp",EDGE,"E404.MirrorCS"),sQuery(id+"F3.wireOp",EDGE,"E405.MirrorCS"),sQuery(id+"F3.wireOp",EDGE,"E406"),sQuery(id+"F3.wireOp",EDGE,"E408.MirrorCS"),sQuery(id+"F3.wireOp",EDGE,"E409.MirrorCS"),sQuery(id+"F3.wireOp",EDGE,"E410"),sQuery(id+"F3.wireOp",EDGE,"E411.MirrorCS"),sQuery(id+"F3.wireOp",EDGE,"E412.MirrorCS"),sQuery(id+"F3.wireOp",EDGE,"E413.MirrorCS"),sQuery(id+"F3.wireOp",EDGE,"E414.MirrorCS"),sQuery(id+"F3.wireOp",EDGE,"E415.MirrorCS"),sQuery(id+"F3.wireOp",EDGE,"E416.MirrorCS"),sQuery(id+"F3.wireOp",EDGE,"E417.MirrorCS"),sQuery(id+"F3.wireOp",EDGE,"E418.MirrorCS"),sQuery(id+"F3.wireOp",EDGE,"E421"),sQuery(id+"F3.wireOp",EDGE,"E422.filletArc"),sQuery(id+"F3.wireOp",EDGE,"E423.MirrorCS"),sQuery(id+"F3.wireOp",EDGE,"E424.MirrorCS"),sQuery(id+"F3.wireOp",EDGE,"E425"),sQuery(id+"F3.wireOp",EDGE,"E428"),sQuery(id+"F3.wireOp",EDGE,"E429.filletArc"),sQuery(id+"F3.wireOp",EDGE,"E430.filletArc"),sQuery(id+"F3.wireOp",EDGE,"E431.MirrorCS"),sQuery(id+"F3.wireOp",EDGE,"E432.MirrorCS"),sQuery(id+"F3.wireOp",EDGE,"E433.MirrorCS"),sQuery(id+"F3.wireOp",EDGE,"E434.MirrorCS"),sQuery(id+"F3.wireOp",EDGE,"E437"),sQuery(id+"F3.wireOp",EDGE,"E440.MirrorCS"),sQuery(id+"F3.wireOp",EDGE,"E441"),sQuery(id+"F3.wireOp",EDGE,"E442"),sQuery(id+"F3.wireOp",EDGE,"E443.MirrorCS"),sQuery(id+"F3.wireOp",EDGE,"E444"),sQuery(id+"F3.wireOp",EDGE,"E445")])],"isStart":false});
            var sketch = newSketch(context, id + "F13", { "sketchPlane" : qUnion([Q0])});
            skLineSegment(sketch, "E810", {"start": v(-35.6, -40.59) * mm, "end": v(-54.2, -21.99) * mm, "construction": true});
            skLineSegment(sketch, "E811", {"start": v(-35.6, -40.59) * mm, "end": v(-35.6, -12.85) * mm, "construction": true});
            skArc(sketch, "E812", {"start": v(-37.4, -37) * mm, "mid": v(-38.44, -37.76) * mm, "end": v(-39.19, -38.8) * mm});
            skLineSegment(sketch, "E813", {"start": v(-35.6, -40.59) * mm, "end": v(-35.6, 6.72) * mm, "construction": true});
            skArc(sketch, "E814.trimOffspring", {"start": v(-32, -38.87) * mm, "mid": v(-32.78, -37.76) * mm, "end": v(-33.9, -36.98) * mm});
            skArc(sketch, "E815.trimOffspring", {"start": v(-33.82, -44.17) * mm, "mid": v(-32.78, -43.42) * mm, "end": v(-32.03, -42.37) * mm});
            skArc(sketch, "E816.trimOffspring", {"start": v(-39.22, -42.3) * mm, "mid": v(-38.44, -43.42) * mm, "end": v(-37.32, -44.2) * mm});
            skArc(sketch, "E817", {"start": v(-27.83, -34.93) * mm, "mid": v(-27.83, -32.81) * mm, "end": v(-29.95, -32.81) * mm});
            skPoint(sketch, "E818.center.orphan", {"position": v(-29.95, -34.93) * mm});
            skArc(sketch, "E819", {"start": v(-31.01, -33.87) * mm, "mid": v(-31.01, -36) * mm, "end": v(-28.89, -36) * mm});
            skLineSegment(sketch, "E820", {"start": v(-27.83, -34.93) * mm, "end": v(-28.89, -36) * mm});
            skLineSegment(sketch, "E821", {"start": v(-29.95, -32.81) * mm, "end": v(-31.01, -33.87) * mm});
            skArc(sketch, "E822", {"start": v(-24.65, -36.2) * mm, "mid": v(-27.02, -32.5) * mm, "end": v(-30.57, -29.92) * mm});
            skLineSegment(sketch, "E823", {"start": v(-33.9, -36.98) * mm, "end": v(-33.9, -32.98) * mm});
            skLineSegment(sketch, "E824", {"start": v(-37.4, -37) * mm, "end": v(-37.4, -33) * mm});
            skArc(sketch, "E825", {"start": v(-33.9, -32.98) * mm, "mid": v(-35.66, -31.23) * mm, "end": v(-37.4, -33) * mm});
            skArc(sketch, "E826", {"start": v(-33.04, -30.76) * mm, "mid": v(-34.31, -30.5) * mm, "end": v(-35.6, -30.43) * mm});
            skLineSegment(sketch, "E827", {"start": v(-31.7, -30.12) * mm, "end": v(-32.08, -30.5) * mm});
            skPoint(sketch, "E828.visualSharp", {"position": v(-32.5, -30.91) * mm});
            skArc(sketch, "E828.filletArc", {"start": v(-33.04, -30.76) * mm, "mid": v(-32.52, -30.75) * mm, "end": v(-32.08, -30.5) * mm});
            skPoint(sketch, "E829.visualSharp", {"position": v(-31.22, -29.64) * mm});
            skArc(sketch, "E829.filletArc", {"start": v(-30.57, -29.92) * mm, "mid": v(-31.16, -29.84) * mm, "end": v(-31.7, -30.12) * mm});
            skLineSegment(sketch, "E830.MirrorCS", {"start": v(-25.14, -36.68) * mm, "end": v(-25.51, -37.06) * mm});
            skArc(sketch, "E831.MirrorCS", {"start": v(-25.77, -38.02) * mm, "mid": v(-25.77, -37.5) * mm, "end": v(-25.51, -37.06) * mm});
            skArc(sketch, "E832.MirrorCS", {"start": v(-25.77, -38.02) * mm, "mid": v(-25.53, -39.3) * mm, "end": v(-25.44, -40.59) * mm});
            skPoint(sketch, "E833.MirrorP", {"position": v(-25.93, -37.48) * mm});
            skPoint(sketch, "E834.MirrorP", {"position": v(-24.65, -36.2) * mm});
            skArc(sketch, "E835.MirrorCS", {"start": v(-24.94, -35.55) * mm, "mid": v(-24.86, -36.15) * mm, "end": v(-25.14, -36.68) * mm});
            skLineSegment(sketch, "E836.MirrorCS", {"start": v(-32, -38.87) * mm, "end": v(-28, -38.87) * mm});
            skArc(sketch, "E837.MirrorCS", {"start": v(-28, -38.87) * mm, "mid": v(-26.24, -40.64) * mm, "end": v(-28.03, -42.37) * mm});
            skLineSegment(sketch, "E838.MirrorCS", {"start": v(-32.03, -42.37) * mm, "end": v(-28.03, -42.37) * mm});
            skLineSegment(sketch, "E839.MirrorCS", {"start": v(-39.51, -51.06) * mm, "end": v(-39.14, -50.68) * mm});
            skLineSegment(sketch, "E840.MirrorCS", {"start": v(-46.08, -44.5) * mm, "end": v(-45.7, -44.12) * mm});
            skArc(sketch, "E841.MirrorCS", {"start": v(-45.44, -43.16) * mm, "mid": v(-45.44, -43.67) * mm, "end": v(-45.7, -44.12) * mm});
            skPoint(sketch, "E842.MirrorP", {"position": v(-40, -51.54) * mm});
            skArc(sketch, "E843.MirrorCS", {"start": v(-46.28, -45.63) * mm, "mid": v(-46.36, -45.03) * mm, "end": v(-46.08, -44.5) * mm});
            skArc(sketch, "E844.MirrorCS", {"start": v(-40.65, -51.26) * mm, "mid": v(-40.05, -51.34) * mm, "end": v(-39.51, -51.06) * mm});
            skArc(sketch, "E845.MirrorCS", {"start": v(-38.18, -50.42) * mm, "mid": v(-38.7, -50.43) * mm, "end": v(-39.14, -50.68) * mm});
            skArc(sketch, "E846.MirrorCS", {"start": v(-43.22, -42.3) * mm, "mid": v(-44.97, -40.54) * mm, "end": v(-43.19, -38.8) * mm});
            skArc(sketch, "E847.MirrorCS", {"start": v(-45.44, -43.16) * mm, "mid": v(-45.69, -41.88) * mm, "end": v(-45.77, -40.59) * mm});
            skPoint(sketch, "E848.MirrorP", {"position": v(-45.28, -43.7) * mm});
            skLineSegment(sketch, "E849.MirrorCS", {"start": v(-41.26, -48.37) * mm, "end": v(-40.2, -47.3) * mm});
            skArc(sketch, "E850.MirrorCS", {"start": v(-37.32, -44.2) * mm, "mid": v(-38.44, -43.42) * mm, "end": v(-39.22, -42.3) * mm});
            skLineSegment(sketch, "E851.MirrorCS", {"start": v(-43.39, -46.25) * mm, "end": v(-42.32, -45.19) * mm});
            skArc(sketch, "E852.MirrorCS", {"start": v(-42.32, -45.19) * mm, "mid": v(-40.2, -45.19) * mm, "end": v(-40.2, -47.3) * mm});
            skPoint(sketch, "E853.MirrorP", {"position": v(-46.56, -44.98) * mm});
            skArc(sketch, "E854.MirrorCS", {"start": v(-38.18, -50.42) * mm, "mid": v(-36.9, -50.67) * mm, "end": v(-35.6, -50.75) * mm});
            skLineSegment(sketch, "E855.MirrorCS", {"start": v(-39.22, -42.3) * mm, "end": v(-43.22, -42.3) * mm});
            skPoint(sketch, "E856.MirrorP", {"position": v(-38.72, -50.27) * mm});
            skArc(sketch, "E857.MirrorCS", {"start": v(-41.26, -48.37) * mm, "mid": v(-43.39, -48.37) * mm, "end": v(-43.39, -46.25) * mm});
            skArc(sketch, "E858.MirrorCS", {"start": v(-37.32, -48.2) * mm, "mid": v(-35.56, -49.95) * mm, "end": v(-33.82, -48.17) * mm});
            skLineSegment(sketch, "E859.MirrorCS", {"start": v(-37.32, -44.2) * mm, "end": v(-37.32, -48.2) * mm});
            skLineSegment(sketch, "E860.MirrorCS", {"start": v(-39.19, -38.8) * mm, "end": v(-43.19, -38.8) * mm});
            skLineSegment(sketch, "E861.MirrorCS", {"start": v(-33.82, -44.17) * mm, "end": v(-33.82, -48.17) * mm});
            skArc(sketch, "E862.MirrorCS", {"start": v(-40, -51.54) * mm, "mid": v(-43.7, -49.18) * mm, "end": v(-46.28, -45.63) * mm});
            skLineSegment(sketch, "E863.MirrorCS", {"start": v(-25.14, -44.5) * mm, "end": v(-25.51, -44.12) * mm});
            skLineSegment(sketch, "E864.MirrorCS", {"start": v(-31.7, -51.06) * mm, "end": v(-32.08, -50.68) * mm});
            skArc(sketch, "E865.MirrorCS", {"start": v(-25.77, -43.16) * mm, "mid": v(-25.77, -43.67) * mm, "end": v(-25.51, -44.12) * mm});
            skArc(sketch, "E866.MirrorCS", {"start": v(-30.57, -51.26) * mm, "mid": v(-31.16, -51.34) * mm, "end": v(-31.7, -51.06) * mm});
            skArc(sketch, "E867.MirrorCS", {"start": v(-24.94, -45.63) * mm, "mid": v(-24.86, -45.03) * mm, "end": v(-25.14, -44.5) * mm});
            skPoint(sketch, "E868.MirrorP", {"position": v(-24.65, -44.98) * mm});
            skArc(sketch, "E869.MirrorCS", {"start": v(-33.04, -50.42) * mm, "mid": v(-32.52, -50.43) * mm, "end": v(-32.08, -50.68) * mm});
            skArc(sketch, "E870.MirrorCS", {"start": v(-33.04, -50.42) * mm, "mid": v(-34.31, -50.67) * mm, "end": v(-35.6, -50.75) * mm});
            skLineSegment(sketch, "E871.MirrorCS", {"start": v(-27.83, -46.25) * mm, "end": v(-28.89, -45.19) * mm});
            skPoint(sketch, "E872.MirrorP", {"position": v(-32.5, -50.27) * mm});
            skArc(sketch, "E873.MirrorCS", {"start": v(-24.94, -45.63) * mm, "mid": v(-27.26, -48.93) * mm, "end": v(-30.57, -51.26) * mm});
            skPoint(sketch, "E874.MirrorP", {"position": v(-31.22, -51.54) * mm});
            skPoint(sketch, "E875.MirrorP", {"position": v(-29.95, -46.25) * mm});
            skArc(sketch, "E876.MirrorCS", {"start": v(-25.77, -43.16) * mm, "mid": v(-25.53, -41.88) * mm, "end": v(-25.44, -40.59) * mm});
            skPoint(sketch, "E877.MirrorP", {"position": v(-25.93, -43.7) * mm});
            skLineSegment(sketch, "E878.MirrorCS", {"start": v(-29.95, -48.37) * mm, "end": v(-31.01, -47.3) * mm});
            skArc(sketch, "E879.MirrorCS", {"start": v(-27.83, -46.25) * mm, "mid": v(-27.83, -48.37) * mm, "end": v(-29.95, -48.37) * mm});
            skArc(sketch, "E880.MirrorCS", {"start": v(-31.01, -47.3) * mm, "mid": v(-31.01, -45.19) * mm, "end": v(-28.89, -45.19) * mm});
            skLineSegment(sketch, "E881.MirrorCS", {"start": v(-41.26, -32.81) * mm, "end": v(-40.2, -33.87) * mm});
            skLineSegment(sketch, "E882.MirrorCS", {"start": v(-43.39, -34.93) * mm, "end": v(-42.32, -36) * mm});
            skArc(sketch, "E883.MirrorCS", {"start": v(-42.32, -36) * mm, "mid": v(-40.2, -36) * mm, "end": v(-40.2, -33.87) * mm});
            skArc(sketch, "E884.MirrorCS", {"start": v(-41.26, -32.81) * mm, "mid": v(-43.39, -32.81) * mm, "end": v(-43.39, -34.93) * mm});
            skArc(sketch, "E885.MirrorCS", {"start": v(-38.18, -30.76) * mm, "mid": v(-36.9, -30.5) * mm, "end": v(-35.6, -30.43) * mm});
            skLineSegment(sketch, "E886.MirrorCS", {"start": v(-35.6, -40.59) * mm, "end": v(-35.6, -87.9) * mm, "construction": true});
            skLineSegment(sketch, "E887.MirrorCS", {"start": v(-46.08, -36.68) * mm, "end": v(-45.7, -37.06) * mm});
            skArc(sketch, "E888.MirrorCS", {"start": v(-45.44, -38.02) * mm, "mid": v(-45.44, -37.5) * mm, "end": v(-45.7, -37.06) * mm});
            skPoint(sketch, "E889.MirrorP", {"position": v(-45.28, -37.48) * mm});
            skPoint(sketch, "E890.MirrorP", {"position": v(-46.56, -36.2) * mm});
            skArc(sketch, "E891.MirrorCS", {"start": v(-45.44, -38.02) * mm, "mid": v(-45.69, -39.3) * mm, "end": v(-45.77, -40.59) * mm});
            skLineSegment(sketch, "E892.MirrorCS", {"start": v(-39.51, -30.12) * mm, "end": v(-39.14, -30.5) * mm});
            skArc(sketch, "E893.MirrorCS", {"start": v(-40.65, -29.92) * mm, "mid": v(-40.05, -29.84) * mm, "end": v(-39.51, -30.12) * mm});
            skArc(sketch, "E894.MirrorCS", {"start": v(-38.18, -30.76) * mm, "mid": v(-38.7, -30.75) * mm, "end": v(-39.14, -30.5) * mm});
            skPoint(sketch, "E895.MirrorP", {"position": v(-40, -29.64) * mm});
            skPoint(sketch, "E896.MirrorP", {"position": v(-38.72, -30.91) * mm});
            skArc(sketch, "E897.MirrorCS", {"start": v(-40.65, -29.92) * mm, "mid": v(-43.95, -32.25) * mm, "end": v(-46.28, -35.55) * mm});
            skArc(sketch, "E898.MirrorCS", {"start": v(-46.28, -35.55) * mm, "mid": v(-46.36, -36.15) * mm, "end": v(-46.08, -36.68) * mm});
            skLineSegment(sketch, "E899.0", {"start": v(-31.01, -33.87) * mm, "end": v(-28.89, -36) * mm, "construction": true});
            skLineSegment(sketch, "E900.0", {"start": v(-29.95, -32.81) * mm, "end": v(-27.83, -34.93) * mm, "construction": true});
            skSolve(sketch);
        }
        {
            var Q0;
            Q0 = qSketchRegion(id + "F12", true);
            extrude(context, id + "F14", {"entities" : qUnion([Q0]), "operationType" : NewBodyOperationType.ADD, "depth" : 0.8 * mm, "offsetDistance" : 25 * mm});
        }
        {
            var Q0;
            Q0 = qSketchRegion(id + "F13", true);
            extrude(context, id + "F15", {"entities" : qUnion([Q0]), "operationType" : NewBodyOperationType.ADD, "depth" : 0.8 * mm, "offsetDistance" : 25 * mm});
        }
        {
            var Q0;
            Q0 = qSketchRegion(id + "F0", true);
            extrude(context, id + "F16", {"entities" : qUnion([Q0]), "operationType" : NewBodyOperationType.ADD, "depth" : 25 * mm, "offsetDistance" : 25 * mm});
        }
    });
